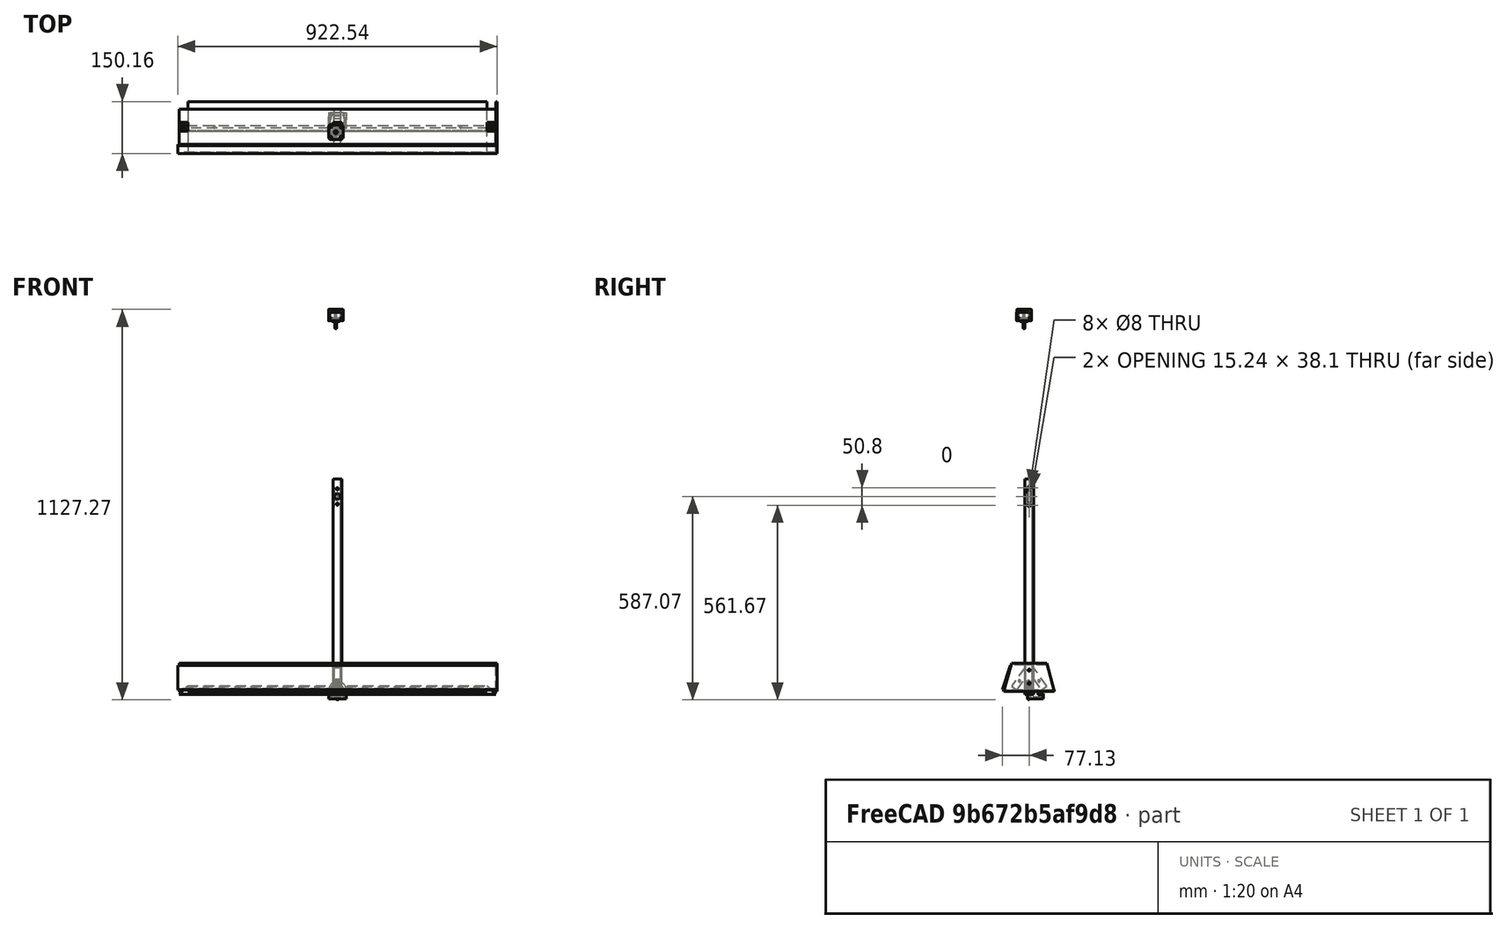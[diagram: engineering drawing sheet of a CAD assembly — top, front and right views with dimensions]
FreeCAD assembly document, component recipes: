
FREECAD ASSEMBLY — COMPONENT RECIPES ("Frame")

This assembly document has 15 components, labeled P0..P14 below (a component is one placed body or linked part). 14 of them carry a construction recipe — the FreeCAD feature program that regenerates the part from scratch, quoted from this document or its linked companion documents; the rest are supplied as boundary geometry only. No exploded tour is included for this assembly.
COMPONENT P0 — recipe-attached ("Base Extrusion", modeled in this document).
Construction recipe (the document's own serialized feature program — sketch geometry with constraints, then the solid features built on it; lengths are millimeters unless a unit is written):

FEATURE [Sketcher::SketchObject] Sketch
  FullyConstrained = true
  MapMode = 5
  Support = -> [XY_Plane]
  sketch-geometry (15):
    g0: LineSegment StartX=-12.7 StartY=-12.7 StartZ=0 EndX=-12.7 EndY=12.7 EndZ=0
    g1: LineSegment StartX=-12.7 StartY=12.7 StartZ=0 EndX=12.7 EndY=12.7 EndZ=0
    g2: LineSegment StartX=12.7 StartY=12.7 StartZ=0 EndX=12.7 EndY=-12.7 EndZ=0
    g3: LineSegment StartX=12.7 StartY=-12.7 StartZ=0 EndX=-12.7 EndY=-12.7 EndZ=0
    g4: GeomPoint X=0 Y=0 Z=0
    g5: ArcOfCircle CenterX=-6.35 CenterY=-6.35 CenterZ=0 NormalX=0 NormalY=0 NormalZ=1 AngleXU=0 Radius=3.175 StartAngle=3.14159 EndAngle=4.71239
    g6: LineSegment StartX=-9.525 StartY=-6.35 StartZ=0 EndX=-9.525 EndY=6.35 EndZ=0
    g7: ArcOfCircle CenterX=-6.35 CenterY=6.35 CenterZ=0 NormalX=0 NormalY=0 NormalZ=1 AngleXU=0 Radius=3.175 StartAngle=1.5708 EndAngle=3.14159
    g8: LineSegment StartX=-6.35 StartY=9.525 StartZ=0 EndX=6.35 EndY=9.525 EndZ=0
    g9: ArcOfCircle CenterX=6.35 CenterY=6.35 CenterZ=0 NormalX=0 NormalY=0 NormalZ=1 AngleXU=0 Radius=3.175 StartAngle=3e-16 EndAngle=1.5708
    g10: LineSegment StartX=9.525 StartY=6.35 StartZ=0 EndX=9.525 EndY=-6.35 EndZ=0
    g11: ArcOfCircle CenterX=6.35 CenterY=-6.35 CenterZ=0 NormalX=0 NormalY=0 NormalZ=1 AngleXU=0 Radius=3.175 StartAngle=4.71239 EndAngle=6.28319
    g12: LineSegment StartX=6.35 StartY=-9.525 StartZ=0 EndX=-6.35 EndY=-9.525 EndZ=0
    g13: GeomPoint X=-9.525 Y=-9.525 Z=0
    g14: GeomPoint X=9.525 Y=9.525 Z=0
  constraints (35):
    c: Coincident(g0,g1)
    c: Coincident(g1,g2)
    c: Coincident(g2,g3)
    c: Coincident(g3,g0)
    c: Horizontal(g1)
    c: Horizontal(g3)
    c: Vertical(g0)
    c: Vertical(g2)
    c: Symmetric(g1,g0,g4)
    c: Coincident(g4,g-1)
    c: Equal(g1,g2)
    c: Distance(g1) = 25.4
    c: Tangent(g5,g6) = 1.5708
    c: Tangent(g6,g7) = 1.5708
    c: Tangent(g7,g8) = 1.5708
    c: Tangent(g8,g9) = 1.5708
    c: Tangent(g9,g10) = 1.5708
    c: Tangent(g10,g11) = 1.5708
    c: Tangent(g11,g12) = 1.5708
    c: Tangent(g12,g5) = 1.5708
    c: Horizontal(g8)
    c: Horizontal(g12)
    c: Vertical(g6)
    c: Vertical(g10)
    c: Equal(g5,g7)
    c: Equal(g7,g9)
    c: Equal(g9,g11)
    c: PointOnObject(g13,g6)
    c: PointOnObject(g13,g12)
    c: PointOnObject(g14,g8)
    c: PointOnObject(g14,g10)
    c: Radius(g9) = 3.175
    c: Symmetric(g7,g11,g4)
    c: Distance(g7,g1) = 3.175
    c: Equal(g8,g6)
FEATURE [PartDesign::Pad] Pad
  Direction = (0,0,1)
  Length = 609.6
  Length2 = 10
  Profile = -> Sketch
  ReferenceAxis = -> Sketch [N_Axis]
  Type = 0
FEATURE [PartDesign::Body] Body  label="Base Extrusion"
  Group = -> [Sketch,Pad]
  Origin = -> Origin
  Tip = -> Pad
COMPONENT P1 — recipe-attached ("Motor Extrusion", modeled in this document).
Construction recipe (the document's own serialized feature program — sketch geometry with constraints, then the solid features built on it; lengths are millimeters unless a unit is written):

FEATURE [Sketcher::SketchObject] Sketch001
  FullyConstrained = true
  MapMode = 5
  Support = -> [XY_Plane001]
  sketch-geometry (15):
    g0: LineSegment StartX=-12.7 StartY=-12.7 StartZ=0 EndX=-12.7 EndY=12.7 EndZ=0
    g1: LineSegment StartX=-12.7 StartY=12.7 StartZ=0 EndX=12.7 EndY=12.7 EndZ=0
    g2: LineSegment StartX=12.7 StartY=12.7 StartZ=0 EndX=12.7 EndY=-12.7 EndZ=0
    g3: LineSegment StartX=12.7 StartY=-12.7 StartZ=0 EndX=-12.7 EndY=-12.7 EndZ=0
    g4: GeomPoint X=0 Y=0 Z=0
    g5: ArcOfCircle CenterX=-6.35 CenterY=-6.35 CenterZ=0 NormalX=0 NormalY=0 NormalZ=1 AngleXU=0 Radius=3.175 StartAngle=3.14159 EndAngle=4.71239
    g6: LineSegment StartX=-9.525 StartY=-6.35 StartZ=0 EndX=-9.525 EndY=6.35 EndZ=0
    g7: ArcOfCircle CenterX=-6.35 CenterY=6.35 CenterZ=0 NormalX=0 NormalY=0 NormalZ=1 AngleXU=0 Radius=3.175 StartAngle=1.5708 EndAngle=3.14159
    g8: LineSegment StartX=-6.35 StartY=9.525 StartZ=0 EndX=6.35 EndY=9.525 EndZ=0
    g9: ArcOfCircle CenterX=6.35 CenterY=6.35 CenterZ=0 NormalX=0 NormalY=0 NormalZ=1 AngleXU=0 Radius=3.175 StartAngle=3e-16 EndAngle=1.5708
    g10: LineSegment StartX=9.525 StartY=6.35 StartZ=0 EndX=9.525 EndY=-6.35 EndZ=0
    g11: ArcOfCircle CenterX=6.35 CenterY=-6.35 CenterZ=0 NormalX=0 NormalY=0 NormalZ=1 AngleXU=0 Radius=3.175 StartAngle=4.71239 EndAngle=6.28319
    g12: LineSegment StartX=6.35 StartY=-9.525 StartZ=0 EndX=-6.35 EndY=-9.525 EndZ=0
    g13: GeomPoint X=-9.525 Y=-9.525 Z=0
    g14: GeomPoint X=9.525 Y=9.525 Z=0
  constraints (35):
    c: Coincident(g0,g1)
    c: Coincident(g1,g2)
    c: Coincident(g2,g3)
    c: Coincident(g3,g0)
    c: Horizontal(g1)
    c: Horizontal(g3)
    c: Vertical(g0)
    c: Vertical(g2)
    c: Symmetric(g1,g0,g4)
    c: Coincident(g4,g-1)
    c: Equal(g1,g2)
    c: Distance(g1) = 25.4
    c: Tangent(g5,g6) = 1.5708
    c: Tangent(g6,g7) = 1.5708
    c: Tangent(g7,g8) = 1.5708
    c: Tangent(g8,g9) = 1.5708
    c: Tangent(g9,g10) = 1.5708
    c: Tangent(g10,g11) = 1.5708
    c: Tangent(g11,g12) = 1.5708
    c: Tangent(g12,g5) = 1.5708
    c: Horizontal(g8)
    c: Horizontal(g12)
    c: Vertical(g6)
    c: Vertical(g10)
    c: Equal(g5,g7)
    c: Equal(g7,g9)
    c: Equal(g9,g11)
    c: PointOnObject(g13,g6)
    c: PointOnObject(g13,g12)
    c: PointOnObject(g14,g8)
    c: PointOnObject(g14,g10)
    c: Radius(g9) = 3.175
    c: Symmetric(g7,g11,g4)
    c: Distance(g7,g1) = 3.175
    c: Equal(g8,g6)
FEATURE [PartDesign::Pad] Pad001
  Direction = (0,0,1)
  Length = 609.6
  Length2 = 10
  Profile = -> Sketch001
  ReferenceAxis = -> Sketch001 [N_Axis]
  Type = 0
FEATURE [Sketcher::SketchObject] Sketch002
  ExternalGeometry = -> [Pad001]
  FullyConstrained = true
  MapMode = 5
  Placement = pos=(0,12.7,0) rot=(0,0.707107,0.707107;3.14159rad)
  Support = -> [Pad001]
  sketch-geometry (8):
    g0: LineSegment StartX=0 StartY=580.72 StartZ=0 EndX=-21.9203 EndY=558.8 EndZ=0
    g1: LineSegment StartX=-21.9203 StartY=558.8 StartZ=0 EndX=0 EndY=536.88 EndZ=0
    g2: LineSegment StartX=0 StartY=536.88 StartZ=0 EndX=21.9203 EndY=558.8 EndZ=0
    g3: LineSegment StartX=21.9203 StartY=558.8 StartZ=0 EndX=0 EndY=580.72 EndZ=0
    g4: LineSegment StartX=21.9203 StartY=558.8 StartZ=0 EndX=-21.9203 EndY=558.8 EndZ=0
    g5: Circle CenterX=0 CenterY=558.8 CenterZ=0 NormalX=0 NormalY=0 NormalZ=1 AngleXU=0 Radius=8.89
    g6: Circle CenterX=0 CenterY=580.72 CenterZ=0 NormalX=0 NormalY=0 NormalZ=1 AngleXU=0 Radius=1.6
    g7: Circle CenterX=0 CenterY=536.88 CenterZ=0 NormalX=0 NormalY=0 NormalZ=1 AngleXU=0 Radius=1.6
  constraints (21):
    c: PointOnObject(g0,g-2)
    c: Coincident(g1,g0)
    c: PointOnObject(g1,g-2)
    c: Coincident(g2,g1)
    c: Coincident(g3,g2)
    c: Coincident(g3,g0)
    c: Perpendicular(g3,g0)
    c: Perpendicular(g2,g1)
    c: Perpendicular(g1,g0)
    c: Coincident(g4,g2)
    c: Coincident(g4,g0)
    c: Horizontal(g4)
    c: Distance(g3) = 31
    c: PointOnObject(g5,g4)
    c: Coincident(g6,g0)
    c: Coincident(g7,g1)
    c: PointOnObject(g5,g-2)
    c: Equal(g7,g6)
    c: Diameter(g6) = 3.2
    c: Diameter(g5) = 17.78
    c: Distance(g5,g-3) = 50.8
FEATURE [PartDesign::Pocket] Pocket
  BaseFeature = -> Pad001
  Direction = (0,-1,2e-16)
  Length = 5.08
  Length2 = 5
  Profile = -> Sketch002
  ReferenceAxis = -> Sketch002 [N_Axis]
  Type = 0
FEATURE [Sketcher::SketchObject] Sketch003
  ExternalGeometry = -> [Pocket]
  FullyConstrained = true
  MapMode = 5
  Placement = pos=(-12.7,0,0) rot=(0.57735,-0.57735,-0.57735;2.0944rad)
  Support = -> [Pocket]
  sketch-geometry (2):
    g0: Circle CenterX=0 CenterY=584.2 CenterZ=0 NormalX=0 NormalY=0 NormalZ=1 AngleXU=0 Radius=4
    g1: Circle CenterX=0 CenterY=533.4 CenterZ=0 NormalX=0 NormalY=0 NormalZ=1 AngleXU=0 Radius=4
  constraints (6):
    c: PointOnObject(g0,g-2)
    c: PointOnObject(g1,g-2)
    c: Equal(g1,g0)
    c: Diameter(g0) = 8
    c: Distance(g0,g1) = 50.8
    c: Distance(g0,g-3) = 25.4
FEATURE [PartDesign::Pocket] Pocket001
  BaseFeature = -> Pocket
  Direction = (1,0,0)
  Length = 5
  Length2 = 5
  Profile = -> Sketch003
  ReferenceAxis = -> Sketch003 [N_Axis]
  Type = 1
FEATURE [Sketcher::SketchObject] Sketch004
  ExternalGeometry = -> [Pocket001]
  FullyConstrained = true
  MapMode = 5
  Placement = pos=(0,-12.7,0) rot=(1,0,0;1.5708rad)
  Support = -> [Pocket001]
  sketch-geometry (3):
    g0: LineSegment StartX=12.7 StartY=0 StartZ=0 EndX=-12.7 EndY=0 EndZ=0
    g1: LineSegment StartX=-12.7 StartY=0 StartZ=0 EndX=-12.7 EndY=25.4 EndZ=0
    g2: LineSegment StartX=-12.7 StartY=25.4 StartZ=0 EndX=12.7 EndY=0 EndZ=0
  constraints (7):
    c: Coincident(g0,g-3)
    c: Coincident(g1,g0)
    c: Vertical(g1)
    c: Coincident(g2,g1)
    c: Coincident(g2,g0)
    c: Equal(g1,g0)
    c: Coincident(g-4,g0)
FEATURE [PartDesign::Pocket] Pocket002
  BaseFeature = -> Pocket001
  Direction = (0,1,-2e-16)
  Length = 5
  Length2 = 5
  Profile = -> Sketch004
  ReferenceAxis = -> Sketch004 [N_Axis]
  Type = 1
FEATURE [PartDesign::CoordinateSystem] Local_CS  label="MotorWeldLCS"
  AttacherType = Attacher::AttachEngine3D
  MapMode = 45
  Placement = pos=(2.4e-14,-3.168e-13,12.7) rot=(0.357407,0.357407,0.862856;1.71777rad)
  Support = -> [Pocket002]
FEATURE [PartDesign::CoordinateSystem] Local_CS001  label="MotorLCS"
  AttacherType = Attacher::AttachEngine3D
  MapMode = 11
  Placement = pos=(0,12.7,558.8) rot=(0.57735,0.57735,0.57735;4.18879rad)
  Support = -> [Pocket002]
FEATURE [PartDesign::CoordinateSystem] Local_CS002  label="LowerRailLCS"
  AttacherType = Attacher::AttachEngine3D
  MapMode = 11
  Placement = pos=(12.7,0,533.4) rot=(0,-1,0;1.5708rad)
  Support = -> [Pocket002]
FEATURE [PartDesign::CoordinateSystem] Local_CS003  label="UpperRailLCS"
  AttacherType = Attacher::AttachEngine3D
  MapMode = 11
  Placement = pos=(12.7,0,584.2) rot=(0,-1,0;1.5708rad)
  Support = -> [Pocket002]
FEATURE [Sketcher::SketchObject] Sketch010
  ExternalGeometry = -> [Pocket002]
  FullyConstrained = true
  MapMode = 5
  Placement = pos=(12.7,0,0) rot=(0.57735,0.57735,0.57735;2.0944rad)
  Support = -> [Pocket002]
  sketch-geometry (12):
    g0: ArcOfCircle CenterX=-2.8575 CenterY=544.513 CenterZ=0 NormalX=0 NormalY=0 NormalZ=1 AngleXU=0 Radius=4.7625 StartAngle=3.14159 EndAngle=4.71239
    g1: LineSegment StartX=-7.62 StartY=544.513 StartZ=0 EndX=-7.62 EndY=573.088 EndZ=0
    g2: ArcOfCircle CenterX=-2.8575 CenterY=573.088 CenterZ=0 NormalX=0 NormalY=0 NormalZ=1 AngleXU=0 Radius=4.7625 StartAngle=1.5708 EndAngle=3.14159
    g3: LineSegment StartX=-2.8575 StartY=577.85 StartZ=0 EndX=2.8575 EndY=577.85 EndZ=0
    g4: ArcOfCircle CenterX=2.8575 CenterY=573.088 CenterZ=0 NormalX=0 NormalY=0 NormalZ=1 AngleXU=0 Radius=4.7625 StartAngle=-5.3e-15 EndAngle=1.5708
    g5: LineSegment StartX=7.62 StartY=573.088 StartZ=0 EndX=7.62 EndY=544.513 EndZ=0
    g6: ArcOfCircle CenterX=2.8575 CenterY=544.513 CenterZ=0 NormalX=0 NormalY=0 NormalZ=1 AngleXU=0 Radius=4.7625 StartAngle=4.71239 EndAngle=6.28319
    g7: LineSegment StartX=2.8575 StartY=539.75 StartZ=0 EndX=-2.8575 EndY=539.75 EndZ=0
    g8: GeomPoint X=-7.62 Y=539.75 Z=0
    g9: GeomPoint X=7.62 Y=577.85 Z=0
    g10: LineSegment StartX=0 StartY=584.2 StartZ=0 EndX=0 EndY=577.85 EndZ=0
    g11: LineSegment StartX=0 StartY=533.4 StartZ=0 EndX=0 EndY=539.75 EndZ=0
  constraints (29):
    c: Tangent(g0,g1) = 1.5708
    c: Tangent(g1,g2) = 1.5708
    c: Tangent(g2,g3) = 1.5708
    c: Tangent(g3,g4) = 1.5708
    c: Tangent(g4,g5) = 1.5708
    c: Tangent(g5,g6) = 1.5708
    c: Tangent(g6,g7) = 1.5708
    c: Tangent(g7,g0) = 1.5708
    c: Horizontal(g3)
    c: Horizontal(g7)
    c: Vertical(g1)
    c: Vertical(g5)
    c: Equal(g0,g2)
    c: Equal(g4,g6)
    c: PointOnObject(g8,g1)
    c: PointOnObject(g8,g7)
    c: PointOnObject(g9,g3)
    c: PointOnObject(g9,g5)
    c: Radius(g4) = 4.7625
    c: Symmetric(g4,g2,g-2)
    c: Distance(g1,g4) = 15.24
    c: Coincident(g10,g-3)
    c: PointOnObject(g10,g3)
    c: Vertical(g10)
    c: Coincident(g11,g-4)
    c: PointOnObject(g11,g7)
    c: Vertical(g11)
    c: Equal(g11,g10)
    c: Distance(g10) = 6.35
FEATURE [PartDesign::Pocket] Pocket006
  BaseFeature = -> Pocket002
  Direction = (-1,0,0)
  Length = 5
  Length2 = 5
  Profile = -> Sketch010
  ReferenceAxis = -> Sketch010 [N_Axis]
  Type = 1
FEATURE [PartDesign::Plane] DatumPlane
  AttachmentOffset = pos=(0,0,-3.175) rot=(0,0,1;0rad)
  Length = 60
  MapMode = 5
  Placement = pos=(-9.525,0,0) rot=(0.57735,-0.57735,-0.57735;2.0944rad)
  ResizeMode = 0
  Support = -> [Pocket006]
  Width = 60
FEATURE [Sketcher::SketchObject] Sketch014
  ExternalGeometry = -> [Pocket006]
  FullyConstrained = true
  MapMode = 5
  Placement = pos=(-9.525,0,0) rot=(0.57735,-0.57735,-0.57735;2.0944rad)
  Support = -> [DatumPlane]
  sketch-geometry (9):
    g0: LineSegment StartX=12.7 StartY=31.75 StartZ=0 EndX=12.7 EndY=64.9627 EndZ=0
    g1: LineSegment StartX=12.7 StartY=64.9627 StartZ=0 EndX=50.5364 EndY=10.9266 EndZ=0
    g2: LineSegment StartX=50.5364 StartY=10.9266 StartZ=0 EndX=34.9316 EndY=0 EndZ=0
    g3: LineSegment StartX=34.9316 StartY=0 StartZ=0 EndX=12.7 EndY=31.75 EndZ=0
    g4: LineSegment StartX=-12.7 StartY=64.9627 StartZ=0 EndX=-12.7 EndY=31.75 EndZ=0
    g5: LineSegment StartX=-12.7 StartY=31.75 StartZ=0 EndX=-34.9316 EndY=-7.1e-15 EndZ=0
    g6: LineSegment StartX=-34.9316 StartY=-7.1e-15 StartZ=0 EndX=-50.5364 EndY=10.9266 EndZ=0
    g7: LineSegment StartX=-50.5364 StartY=10.9266 StartZ=0 EndX=-12.7 EndY=64.9627 EndZ=0
    g8: LineSegment StartX=12.7 StartY=31.75 StartZ=0 EndX=-12.7 EndY=31.75 EndZ=0
  constraints (26):
    c: Vertical(g0)
    c: Coincident(g1,g0)
    c: Coincident(g2,g1)
    c: Coincident(g3,g2)
    c: Coincident(g3,g0)
    c: Vertical(g4)
    c: Coincident(g5,g4)
    c: Coincident(g6,g5)
    c: Coincident(g7,g6)
    c: Coincident(g7,g4)
    c: Equal(g4,g0)
    c: Perpendicular(g6,g5)
    c: Perpendicular(g7,g6)
    c: Perpendicular(g2,g3)
    c: Perpendicular(g1,g2)
    c: Coincident(g8,g0)
    c: Horizontal(g8)
    c: Coincident(g4,g8)
    c: PointOnObject(g4,g-4)
    c: PointOnObject(g0,g-3)
    c: Distance(g-3,g0) = 6.35
    c: Distance(g2) = 19.05
    c: Equal(g6,g2)
    c: Equal(g3,g5)
    c: PointOnObject(g2,g-1)
    c: Angle(g3,g-3) = 2.53073
FEATURE [PartDesign::Pad] Pad004
  BaseFeature = -> Pocket006
  Direction = (-1,0,0)
  Length = 19.05
  Length2 = 10
  Profile = -> Sketch014
  ReferenceAxis = -> Sketch014 [N_Axis]
  Reversed = true
  Type = 0
FEATURE [Sketcher::SketchObject] Sketch020
  ExternalGeometry = -> [Pad004]
  FullyConstrained = true
  MapMode = 5
  Placement = pos=(0,-12.7,0) rot=(1,0,0;1.5708rad)
  Support = -> [Pad004]
  sketch-geometry (2):
    g0: Circle CenterX=0 CenterY=536.88 CenterZ=0 NormalX=0 NormalY=0 NormalZ=1 AngleXU=0 Radius=3.302
    g1: Circle CenterX=0 CenterY=580.72 CenterZ=0 NormalX=0 NormalY=0 NormalZ=1 AngleXU=0 Radius=3.302
  constraints (4):
    c: Coincident(g0,g-5)
    c: Coincident(g1,g-3)
    c: Equal(g1,g0)
    c: Diameter(g1) = 6.604
FEATURE [PartDesign::Pocket] Pocket012
  BaseFeature = -> Pad004
  Direction = (0,1,-2e-16)
  Length = 7.62
  Length2 = 5
  Profile = -> Sketch020
  ReferenceAxis = -> Sketch020 [N_Axis]
  Type = 0
FEATURE [Sketcher::SketchObject] Sketch021
  ExternalGeometry = -> [Pocket012]
  FullyConstrained = true
  MapMode = 5
  Placement = pos=(9.525,0,0) rot=(0.57735,0.57735,0.57735;2.0944rad)
  Support = -> [Pocket012]
  sketch-geometry (4):
    g0: LineSegment StartX=-42.734 StartY=5.46332 StartZ=0 EndX=-28.1652 EndY=26.2698 EndZ=0
    g1: LineSegment StartX=42.734 StartY=5.46332 StartZ=0 EndX=28.1652 EndY=26.2698 EndZ=0
    g2: Circle CenterX=-28.1652 CenterY=26.2698 CenterZ=0 NormalX=0 NormalY=0 NormalZ=1 AngleXU=0 Radius=3.175
    g3: Circle CenterX=28.1652 CenterY=26.2698 CenterZ=0 NormalX=0 NormalY=0 NormalZ=1 AngleXU=0 Radius=3.175
  constraints (10):
    c: Symmetric(g-3,g-3,g0)
    c: Symmetric(g-4,g-4,g1)
    c: Equal(g0,g1)
    c: Perpendicular(g-3,g0)
    c: Perpendicular(g-4,g1)
    c: Distance(g1) = 25.4
    c: Coincident(g2,g0)
    c: Coincident(g3,g1)
    c: Equal(g3,g2)
    c: Diameter(g2) = 6.35
FEATURE [PartDesign::Pocket] Pocket013
  BaseFeature = -> Pocket012
  Direction = (-1,0,0)
  Length = 5
  Length2 = 5
  Profile = -> Sketch021
  ReferenceAxis = -> Sketch021 [N_Axis]
  Type = 1
FEATURE [PartDesign::Body] Body001  label="Motor Extrusion"
  Group = -> [Sketch001,Pad001,Sketch002,Pocket,Sketch003,Pocket001,Sketch004,Pocket002,Local_CS,Local_CS001,Local_CS002,Local_CS003,Sketch010,Pocket006,DatumPlane,Sketch014,Pad004,Sketch020,Pocket012,Sketch021,Pocket013]
  Origin = -> Origin001
  Tip = -> Pocket013
COMPONENT P2 — recipe-attached ("Endplate Extrusion", modeled in this document).
Construction recipe (the document's own serialized feature program — sketch geometry with constraints, then the solid features built on it; lengths are millimeters unless a unit is written):

FEATURE [Sketcher::SketchObject] Sketch005
  FullyConstrained = true
  MapMode = 5
  Support = -> [XY_Plane002]
  sketch-geometry (15):
    g0: LineSegment StartX=-12.7 StartY=-12.7 StartZ=0 EndX=-12.7 EndY=12.7 EndZ=0
    g1: LineSegment StartX=-12.7 StartY=12.7 StartZ=0 EndX=12.7 EndY=12.7 EndZ=0
    g2: LineSegment StartX=12.7 StartY=12.7 StartZ=0 EndX=12.7 EndY=-12.7 EndZ=0
    g3: LineSegment StartX=12.7 StartY=-12.7 StartZ=0 EndX=-12.7 EndY=-12.7 EndZ=0
    g4: GeomPoint X=0 Y=0 Z=0
    g5: ArcOfCircle CenterX=-6.35 CenterY=-6.35 CenterZ=0 NormalX=0 NormalY=0 NormalZ=1 AngleXU=0 Radius=3.175 StartAngle=3.14159 EndAngle=4.71239
    g6: LineSegment StartX=-9.525 StartY=-6.35 StartZ=0 EndX=-9.525 EndY=6.35 EndZ=0
    g7: ArcOfCircle CenterX=-6.35 CenterY=6.35 CenterZ=0 NormalX=0 NormalY=0 NormalZ=1 AngleXU=0 Radius=3.175 StartAngle=1.5708 EndAngle=3.14159
    g8: LineSegment StartX=-6.35 StartY=9.525 StartZ=0 EndX=6.35 EndY=9.525 EndZ=0
    g9: ArcOfCircle CenterX=6.35 CenterY=6.35 CenterZ=0 NormalX=0 NormalY=0 NormalZ=1 AngleXU=0 Radius=3.175 StartAngle=3e-16 EndAngle=1.5708
    g10: LineSegment StartX=9.525 StartY=6.35 StartZ=0 EndX=9.525 EndY=-6.35 EndZ=0
    g11: ArcOfCircle CenterX=6.35 CenterY=-6.35 CenterZ=0 NormalX=0 NormalY=0 NormalZ=1 AngleXU=0 Radius=3.175 StartAngle=4.71239 EndAngle=6.28319
    g12: LineSegment StartX=6.35 StartY=-9.525 StartZ=0 EndX=-6.35 EndY=-9.525 EndZ=0
    g13: GeomPoint X=-9.525 Y=-9.525 Z=0
    g14: GeomPoint X=9.525 Y=9.525 Z=0
  constraints (35):
    c: Coincident(g0,g1)
    c: Coincident(g1,g2)
    c: Coincident(g2,g3)
    c: Coincident(g3,g0)
    c: Horizontal(g1)
    c: Horizontal(g3)
    c: Vertical(g0)
    c: Vertical(g2)
    c: Symmetric(g1,g0,g4)
    c: Coincident(g4,g-1)
    c: Equal(g1,g2)
    c: Distance(g1) = 25.4
    c: Tangent(g5,g6) = 1.5708
    c: Tangent(g6,g7) = 1.5708
    c: Tangent(g7,g8) = 1.5708
    c: Tangent(g8,g9) = 1.5708
    c: Tangent(g9,g10) = 1.5708
    c: Tangent(g10,g11) = 1.5708
    c: Tangent(g11,g12) = 1.5708
    c: Tangent(g12,g5) = 1.5708
    c: Horizontal(g8)
    c: Horizontal(g12)
    c: Vertical(g6)
    c: Vertical(g10)
    c: Equal(g5,g7)
    c: Equal(g7,g9)
    c: Equal(g9,g11)
    c: PointOnObject(g13,g6)
    c: PointOnObject(g13,g12)
    c: PointOnObject(g14,g8)
    c: PointOnObject(g14,g10)
    c: Radius(g9) = 3.175
    c: Symmetric(g7,g11,g4)
    c: Distance(g7,g1) = 3.175
    c: Equal(g8,g6)
FEATURE [PartDesign::Pad] Pad002
  Direction = (0,0,1)
  Length = 609.6
  Length2 = 10
  Profile = -> Sketch005
  ReferenceAxis = -> Sketch005 [N_Axis]
  Type = 0
FEATURE [Sketcher::SketchObject] Sketch006
  ExternalGeometry = -> [Pad002]
  FullyConstrained = true
  MapMode = 5
  Placement = pos=(12.7,0,0) rot=(0.57735,0.57735,0.57735;2.0944rad)
  Support = -> [Pad002]
  sketch-geometry (2):
    g0: Circle CenterX=0 CenterY=584.2 CenterZ=0 NormalX=0 NormalY=0 NormalZ=1 AngleXU=0 Radius=4
    g1: Circle CenterX=0 CenterY=533.4 CenterZ=0 NormalX=0 NormalY=0 NormalZ=1 AngleXU=0 Radius=4
  constraints (6):
    c: PointOnObject(g0,g-2)
    c: PointOnObject(g1,g-2)
    c: Equal(g1,g0)
    c: Diameter(g0) = 8
    c: Distance(g0,g-3) = 25.4
    c: Distance(g0,g1) = 50.8
FEATURE [PartDesign::Pocket] Pocket003
  BaseFeature = -> Pad002
  Direction = (-1,0,0)
  Length = 5
  Length2 = 5
  Profile = -> Sketch006
  ReferenceAxis = -> Sketch006 [N_Axis]
  Type = 1
FEATURE [Sketcher::SketchObject] Sketch007
  ExternalGeometry = -> [Pocket003]
  FullyConstrained = true
  MapMode = 5
  Placement = pos=(0,-12.7,0) rot=(1,0,0;1.5708rad)
  Support = -> [Pocket003]
  sketch-geometry (3):
    g0: LineSegment StartX=12.7 StartY=25.4 StartZ=0 EndX=-12.7 EndY=0 EndZ=0
    g1: LineSegment StartX=12.7 StartY=25.4 StartZ=0 EndX=12.7 EndY=0 EndZ=0
    g2: LineSegment StartX=12.7 StartY=0 StartZ=0 EndX=-12.7 EndY=0 EndZ=0
  constraints (7):
    c: PointOnObject(g0,g-4)
    c: Coincident(g1,g0)
    c: Coincident(g1,g-4)
    c: Coincident(g2,g1)
    c: Coincident(g2,g0)
    c: Equal(g1,g2)
    c: Coincident(g0,g-3)
FEATURE [PartDesign::Pocket] Pocket004
  BaseFeature = -> Pocket003
  Direction = (0,1,-2e-16)
  Length = 5
  Length2 = 5
  Profile = -> Sketch007
  ReferenceAxis = -> Sketch007 [N_Axis]
  Type = 1
FEATURE [PartDesign::CoordinateSystem] Local_CS004  label="EndWeldLCS"
  AttacherType = Attacher::AttachEngine3D
  MapMode = 45
  Placement = pos=(2.49e-14,3.02e-14,12.7) rot=(-0.357407,-0.357407,0.862856;1.71777rad)
  Support = -> [Pocket004]
FEATURE [Sketcher::SketchObject] Sketch011
  ExternalGeometry = -> [Pocket004]
  FullyConstrained = true
  MapMode = 5
  Placement = pos=(-12.7,0,0) rot=(0.57735,-0.57735,-0.57735;2.0944rad)
  Support = -> [Pocket004]
  sketch-geometry (12):
    g0: ArcOfCircle CenterX=-2.8575 CenterY=544.513 CenterZ=0 NormalX=0 NormalY=0 NormalZ=1 AngleXU=0 Radius=4.7625 StartAngle=3.14159 EndAngle=4.71239
    g1: LineSegment StartX=-7.62 StartY=544.513 StartZ=0 EndX=-7.62 EndY=573.087 EndZ=0
    g2: ArcOfCircle CenterX=-2.8575 CenterY=573.087 CenterZ=0 NormalX=0 NormalY=0 NormalZ=1 AngleXU=0 Radius=4.7625 StartAngle=1.5708 EndAngle=3.14159
    g3: LineSegment StartX=-2.8575 StartY=577.85 StartZ=0 EndX=2.8575 EndY=577.85 EndZ=0
    g4: ArcOfCircle CenterX=2.8575 CenterY=573.087 CenterZ=0 NormalX=0 NormalY=0 NormalZ=1 AngleXU=0 Radius=4.7625 StartAngle=-8.9e-15 EndAngle=1.5708
    g5: LineSegment StartX=7.62 StartY=573.087 StartZ=0 EndX=7.62 EndY=544.513 EndZ=0
    g6: ArcOfCircle CenterX=2.8575 CenterY=544.513 CenterZ=0 NormalX=0 NormalY=0 NormalZ=1 AngleXU=0 Radius=4.7625 StartAngle=4.71239 EndAngle=6.28319
    g7: LineSegment StartX=2.8575 StartY=539.75 StartZ=0 EndX=-2.8575 EndY=539.75 EndZ=0
    g8: GeomPoint X=-7.62 Y=539.75 Z=0
    g9: GeomPoint X=7.62 Y=577.85 Z=0
    g10: LineSegment StartX=0 StartY=577.85 StartZ=0 EndX=0 EndY=584.2 EndZ=0
    g11: LineSegment StartX=0 StartY=539.75 StartZ=0 EndX=0 EndY=533.4 EndZ=0
  constraints (29):
    c: Tangent(g0,g1) = 1.5708
    c: Tangent(g1,g2) = 1.5708
    c: Tangent(g2,g3) = 1.5708
    c: Tangent(g3,g4) = 1.5708
    c: Tangent(g4,g5) = 1.5708
    c: Tangent(g5,g6) = 1.5708
    c: Tangent(g6,g7) = 1.5708
    c: Tangent(g7,g0) = 1.5708
    c: Horizontal(g3)
    c: Vertical(g1)
    c: Vertical(g5)
    c: Equal(g0,g2)
    c: Equal(g2,g4)
    c: Equal(g4,g6)
    c: PointOnObject(g8,g1)
    c: PointOnObject(g8,g7)
    c: PointOnObject(g9,g3)
    c: PointOnObject(g9,g5)
    c: Symmetric(g6,g0,g-2)
    c: Radius(g6) = 4.7625
    c: PointOnObject(g10,g3)
    c: Coincident(g10,g-3)
    c: Vertical(g10)
    c: PointOnObject(g11,g7)
    c: Coincident(g11,g-4)
    c: Vertical(g11)
    c: Equal(g11,g10)
    c: Distance(g10) = 6.35
    c: Distance(g4,g1) = 15.24
FEATURE [PartDesign::Pocket] Pocket007
  BaseFeature = -> Pocket004
  Direction = (1,0,0)
  Length = 5
  Length2 = 5
  Profile = -> Sketch011
  ReferenceAxis = -> Sketch011 [N_Axis]
  Type = 1
FEATURE [Sketcher::SketchObject] Sketch012
  ExternalGeometry = -> [Pocket007]
  FullyConstrained = true
  MapMode = 5
  Placement = pos=(0,-12.7,0) rot=(1,0,0;1.5708rad)
  Support = -> [Pocket007]
  sketch-geometry (2):
    g0: Circle CenterX=0 CenterY=558.8 CenterZ=0 NormalX=0 NormalY=0 NormalZ=1 AngleXU=0 Radius=8.255
    g1: LineSegment StartX=0 StartY=558.8 StartZ=0 EndX=-12.7 EndY=558.8 EndZ=0
  constraints (5):
    c: PointOnObject(g0,g-2)
    c: Diameter(g0) = 16.51
    c: Coincident(g1,g0)
    c: Horizontal(g1)
    c: Symmetric(g-3,g-3,g1)
FEATURE [PartDesign::Pocket] Pocket008
  BaseFeature = -> Pocket007
  Direction = (0,1,-2e-16)
  Length = 5.08
  Length2 = 5
  Profile = -> Sketch012
  ReferenceAxis = -> Sketch012 [N_Axis]
  Type = 0
FEATURE [Sketcher::SketchObject] Sketch013
  ExternalGeometry = -> [Pocket008]
  FullyConstrained = true
  MapMode = 5
  Placement = pos=(0,-12.7,0) rot=(1,0,0;1.5708rad)
  Support = -> [Pocket008]
  sketch-geometry (1):
    g0: Circle CenterX=0 CenterY=558.8 CenterZ=0 NormalX=0 NormalY=0 NormalZ=1 AngleXU=0 Radius=1.5875
  constraints (2):
    c: Coincident(g0,g-3)
    c: Diameter(g0) = 3.175
FEATURE [PartDesign::Pocket] Pocket009
  BaseFeature = -> Pocket008
  Direction = (0,1,-2e-16)
  Length = 5
  Length2 = 5
  Profile = -> Sketch013
  ReferenceAxis = -> Sketch013 [N_Axis]
  Type = 1
FEATURE [PartDesign::CoordinateSystem] Local_CS011  label="UpperRail"
  AttacherType = Attacher::AttachEngine3D
  MapMode = 11
  Placement = pos=(-12.7,0,584.2) rot=(0.707107,0,0.707107;3.14159rad)
  Support = -> [Pocket009]
FEATURE [PartDesign::CoordinateSystem] Local_CS012  label="LowerRail"
  AttacherType = Attacher::AttachEngine3D
  MapMode = 11
  Placement = pos=(-12.7,0,533.4) rot=(0.707107,0,0.707107;3.14159rad)
  Support = -> [Pocket009]
FEATURE [PartDesign::CoordinateSystem] Local_CS015  label="Eccentric001"
  AttacherType = Attacher::AttachEngine3D
  MapMode = 11
  Placement = pos=(0,9.525,558.8) rot=(0.57735,-0.57735,0.57735;2.0944rad)
  Support = -> [Pocket009]
FEATURE [PartDesign::Body] Body002  label="Endplate Extrusion"
  Group = -> [Sketch005,Pad002,Sketch006,Pocket003,Sketch007,Pocket004,Local_CS004,Sketch011,Pocket007,Sketch012,Pocket008,Sketch013,Pocket009,Local_CS011,Local_CS012,Local_CS015]
  Origin = -> Origin002
  Tip = -> Pocket009
COMPONENT P3 — recipe-attached ("Lower Extrusion", modeled in this document).
Construction recipe (the document's own serialized feature program — sketch geometry with constraints, then the solid features built on it; lengths are millimeters unless a unit is written):

FEATURE [Sketcher::SketchObject] Sketch008
  FullyConstrained = true
  MapMode = 5
  Placement = pos=(0,0,0) rot=(0.57735,0.57735,0.57735;2.0944rad)
  Support = -> [YZ_Plane003]
  sketch-geometry (15):
    g0: LineSegment StartX=-12.7 StartY=-12.7 StartZ=0 EndX=-12.7 EndY=12.7 EndZ=0
    g1: LineSegment StartX=-12.7 StartY=12.7 StartZ=0 EndX=12.7 EndY=12.7 EndZ=0
    g2: LineSegment StartX=12.7 StartY=12.7 StartZ=0 EndX=12.7 EndY=-12.7 EndZ=0
    g3: LineSegment StartX=12.7 StartY=-12.7 StartZ=0 EndX=-12.7 EndY=-12.7 EndZ=0
    g4: GeomPoint X=0 Y=0 Z=0
    g5: ArcOfCircle CenterX=-6.35 CenterY=-6.35 CenterZ=0 NormalX=0 NormalY=0 NormalZ=1 AngleXU=0 Radius=3.175 StartAngle=3.14159 EndAngle=4.71239
    g6: LineSegment StartX=-9.525 StartY=-6.35 StartZ=0 EndX=-9.525 EndY=6.35 EndZ=0
    g7: ArcOfCircle CenterX=-6.35 CenterY=6.35 CenterZ=0 NormalX=0 NormalY=0 NormalZ=1 AngleXU=0 Radius=3.175 StartAngle=1.5708 EndAngle=3.14159
    g8: LineSegment StartX=-6.35 StartY=9.525 StartZ=0 EndX=6.35 EndY=9.525 EndZ=0
    g9: ArcOfCircle CenterX=6.35 CenterY=6.35 CenterZ=0 NormalX=0 NormalY=0 NormalZ=1 AngleXU=0 Radius=3.175 StartAngle=2e-16 EndAngle=1.5708
    g10: LineSegment StartX=9.525 StartY=6.35 StartZ=0 EndX=9.525 EndY=-6.35 EndZ=0
    g11: ArcOfCircle CenterX=6.35 CenterY=-6.35 CenterZ=0 NormalX=0 NormalY=0 NormalZ=1 AngleXU=0 Radius=3.175 StartAngle=4.71239 EndAngle=6.28319
    g12: LineSegment StartX=6.35 StartY=-9.525 StartZ=0 EndX=-6.35 EndY=-9.525 EndZ=0
    g13: GeomPoint X=-9.525 Y=-9.525 Z=0
    g14: GeomPoint X=9.525 Y=9.525 Z=0
  constraints (35):
    c: Coincident(g0,g1)
    c: Coincident(g1,g2)
    c: Coincident(g2,g3)
    c: Coincident(g3,g0)
    c: Horizontal(g1)
    c: Horizontal(g3)
    c: Vertical(g0)
    c: Vertical(g2)
    c: Symmetric(g1,g0,g4)
    c: Coincident(g4,g-1)
    c: Tangent(g5,g6) = 1.5708
    c: Tangent(g6,g7) = 1.5708
    c: Tangent(g7,g8) = 1.5708
    c: Tangent(g8,g9) = 1.5708
    c: Tangent(g9,g10) = 1.5708
    c: Tangent(g10,g11) = 1.5708
    c: Tangent(g11,g12) = 1.5708
    c: Tangent(g12,g5) = 1.5708
    c: Horizontal(g8)
    c: Horizontal(g12)
    c: Vertical(g6)
    c: Vertical(g10)
    c: Equal(g5,g7)
    c: Equal(g7,g9)
    c: Equal(g9,g11)
    c: PointOnObject(g13,g6)
    c: PointOnObject(g13,g12)
    c: PointOnObject(g14,g8)
    c: PointOnObject(g14,g10)
    c: Equal(g8,g6)
    c: Equal(g1,g0)
    c: Symmetric(g9,g5,g4)
    c: Radius(g11) = 3.175
    c: Distance(g10,g2) = 3.175
    c: Distance(g2) = 25.4
FEATURE [PartDesign::Pad] Pad003  label="OverallLength"
  Direction = (1,-2e-16,3e-16)
  Length = 914.4
  Length2 = 10
  Midplane = true
  Placement = pos=(0,0,0) rot=(0.57735,0.57735,0.57735;2.0944rad)
  Profile = -> Sketch008
  ReferenceAxis = -> Sketch008 [N_Axis]
  Type = 0
FEATURE [Sketcher::SketchObject] Sketch009
  ExternalGeometry = -> [Pad003]
  FullyConstrained = true
  MapMode = 5
  Placement = pos=(-5.6e-15,-12.7,2.8e-15) rot=(-0.57735,-0.57735,0.57735;4.18879rad)
  Support = -> [Pad003]
  sketch-geometry (6):
    g0: LineSegment StartX=12.7 StartY=457.2 StartZ=0 EndX=-12.7 EndY=457.2 EndZ=0
    g1: LineSegment StartX=-12.7 StartY=457.2 StartZ=0 EndX=-12.7 EndY=431.8 EndZ=0
    g2: LineSegment StartX=-12.7 StartY=431.8 StartZ=0 EndX=12.7 EndY=457.2 EndZ=0
    g3: LineSegment StartX=12.7 StartY=-457.2 StartZ=0 EndX=-12.7 EndY=-457.2 EndZ=0
    g4: LineSegment StartX=-12.7 StartY=-457.2 StartZ=0 EndX=-12.7 EndY=-431.8 EndZ=0
    g5: LineSegment StartX=-12.7 StartY=-431.8 StartZ=0 EndX=12.7 EndY=-457.2 EndZ=0
  constraints (14):
    c: Coincident(g0,g-5)
    c: Coincident(g0,g-4)
    c: Coincident(g1,g0)
    c: PointOnObject(g1,g-4)
    c: Coincident(g2,g1)
    c: Coincident(g2,g0)
    c: Coincident(g3,g-3)
    c: Coincident(g3,g-4)
    c: Coincident(g4,g3)
    c: PointOnObject(g4,g-4)
    c: Coincident(g5,g4)
    c: Coincident(g5,g3)
    c: Equal(g1,g0)
    c: Equal(g0,g4)
FEATURE [PartDesign::Pocket] Pocket005
  BaseFeature = -> Pad003
  Direction = (4e-16,1,-2e-16)
  Length = 5
  Length2 = 5
  Placement = pos=(0,0,0) rot=(0.57735,0.57735,0.57735;2.0944rad)
  Profile = -> Sketch009
  ReferenceAxis = -> Sketch009 [N_Axis]
  Type = 1
FEATURE [PartDesign::CoordinateSystem] Local_CS005  label="LeftLCS"
  AttacherType = Attacher::AttachEngine3D
  MapMode = 45
  Placement = pos=(-444.5,3.845e-13,-8.53e-14) rot=(-0.357407,-0.357407,0.862856;1.71777rad)
  Support = -> [Pocket005]
FEATURE [PartDesign::CoordinateSystem] Local_CS006  label="RightLCS"
  AttacherType = Attacher::AttachEngine3D
  MapMode = 45
  Placement = pos=(444.5,-6.185e-13,0) rot=(0.357407,0.357407,0.862856;1.71777rad)
  Support = -> [Pocket005]
FEATURE [PartDesign::CoordinateSystem] Local_CS007
  AttacherType = Attacher::AttachEngine3D
  MapMode = 5
  Placement = pos=(3.6e-15,-5.6e-15,-12.7) rot=(0.707107,0.707107,0;3.14159rad)
  Support = -> [Pocket005]
FEATURE [PartDesign::Body] Body003  label="Lower Extrusion"
  Group = -> [Sketch008,Pad003,Sketch009,Pocket005,Local_CS005,Local_CS006,Local_CS007]
  Origin = -> Origin003
  Tip = -> Pocket005
COMPONENT P4 — geometry summary ("NEMA17"; no construction recipe available for this part):
  bounding box: 55.3 x 42.3 x 42.3 mm
  tessellated surface: 13,432 triangles
  volume: 42580 mm^3 (43% of its bounding box)
  symmetry: 4-fold rotationally symmetric about the z axis
COMPONENT P5 — recipe-attached ("TimingPulley", modeled in this document).
Construction recipe (the document's own serialized feature program — sketch geometry with constraints, then the solid features built on it; lengths are millimeters unless a unit is written):

FEATURE [Sketcher::SketchObject] Sketch015
  FullyConstrained = true
  MapMode = 5
  Support = -> [XY_Plane006]
  sketch-geometry (1):
    g0: Circle CenterX=0 CenterY=0 CenterZ=0 NormalX=0 NormalY=0 NormalZ=1 AngleXU=0 Radius=7.62
  constraints (2):
    c: Coincident(g0,g-1)
    c: Diameter(g0) = 15.24
FEATURE [PartDesign::Pad] Pad005
  Direction = (0,0,1)
  Length = 15.24
  Length2 = 10
  Profile = -> Sketch015
  ReferenceAxis = -> Sketch015 [N_Axis]
  Type = 0
FEATURE [PartDesign::Plane] DatumPlane001
  AttachmentOffset = pos=(0,0,-1.27) rot=(0,0,1;0rad)
  Length = 60
  MapMode = 5
  Placement = pos=(0,0,13.97) rot=(0,0,1;0rad)
  ResizeMode = 0
  Support = -> [Pad005]
  Width = 60
FEATURE [Sketcher::SketchObject] Sketch016
  ExternalGeometry = -> [Pad005]
  FullyConstrained = true
  MapMode = 5
  Placement = pos=(0,0,13.97) rot=(0,0,1;0rad)
  Support = -> [DatumPlane001]
  sketch-geometry (18):
    g0: ArcOfCircle CenterX=0 CenterY=7.62 CenterZ=0 NormalX=0 NormalY=0 NormalZ=1 AngleXU=0 Radius=1.27 StartAngle=3.22502 EndAngle=6.19976
    g1: ArcOfCircle CenterX=0 CenterY=0 CenterZ=0 NormalX=0 NormalY=0 NormalZ=1 AngleXU=0 Radius=7.62 StartAngle=1.40394 EndAngle=1.73766
    g2: ArcOfCircle CenterX=7.62 CenterY=0 CenterZ=0 NormalX=0 NormalY=0 NormalZ=1 AngleXU=0 Radius=1.27 StartAngle=1.65423 EndAngle=4.62896
    g3: ArcOfCircle CenterX=0 CenterY=-7.62 CenterZ=0 NormalX=0 NormalY=0 NormalZ=1 AngleXU=0 Radius=1.27 StartAngle=0.0834301 EndAngle=3.05816
    g4: ArcOfCircle CenterX=-7.62 CenterY=0 CenterZ=0 NormalX=0 NormalY=0 NormalZ=1 AngleXU=0 Radius=1.27 StartAngle=4.79582 EndAngle=7.77055
    g5: ArcOfCircle CenterX=-5.38815 CenterY=5.38815 CenterZ=0 NormalX=0 NormalY=0 NormalZ=1 AngleXU=0 Radius=1.27 StartAngle=4.01042 EndAngle=6.98515
    g6: ArcOfCircle CenterX=5.38815 CenterY=5.38815 CenterZ=0 NormalX=0 NormalY=0 NormalZ=1 AngleXU=0 Radius=1.27 StartAngle=2.43962 EndAngle=5.41436
    g7: ArcOfCircle CenterX=5.38815 CenterY=-5.38815 CenterZ=0 NormalX=0 NormalY=0 NormalZ=1 AngleXU=0 Radius=1.27 StartAngle=0.868828 EndAngle=3.84356
    g8: ArcOfCircle CenterX=-5.38815 CenterY=-5.38815 CenterZ=0 NormalX=0 NormalY=0 NormalZ=1 AngleXU=0 Radius=1.27 StartAngle=5.58122 EndAngle=8.55595
    g9: ArcOfCircle CenterX=0 CenterY=0 CenterZ=0 NormalX=0 NormalY=0 NormalZ=1 AngleXU=0 Radius=7.62 StartAngle=2.18933 EndAngle=2.52305
    g10: ArcOfCircle CenterX=0 CenterY=0 CenterZ=0 NormalX=0 NormalY=0 NormalZ=1 AngleXU=0 Radius=7.62 StartAngle=2.97473 EndAngle=3.30845
    g11: ArcOfCircle CenterX=0 CenterY=0 CenterZ=0 NormalX=0 NormalY=0 NormalZ=1 AngleXU=0 Radius=7.62 StartAngle=3.76013 EndAngle=4.09385
    g12: ArcOfCircle CenterX=0 CenterY=0 CenterZ=0 NormalX=0 NormalY=0 NormalZ=1 AngleXU=0 Radius=7.62 StartAngle=6.11633 EndAngle=6.45005
    g13: ArcOfCircle CenterX=0 CenterY=0 CenterZ=0 NormalX=0 NormalY=0 NormalZ=1 AngleXU=0 Radius=7.62 StartAngle=5.33093 EndAngle=5.66465
    g14: ArcOfCircle CenterX=0 CenterY=0 CenterZ=0 NormalX=0 NormalY=0 NormalZ=1 AngleXU=0 Radius=7.62 StartAngle=0.618538 EndAngle=0.952258
    g15: LineSegment StartX=5.38815 StartY=5.38815 StartZ=0 EndX=-5.38815 EndY=-5.38815 EndZ=0
    g16: LineSegment StartX=5.38815 StartY=-5.38815 StartZ=0 EndX=-5.38815 EndY=5.38815 EndZ=0
    g17: ArcOfCircle CenterX=-1.7e-15 CenterY=3.72e-14 CenterZ=0 NormalX=0 NormalY=0 NormalZ=1 AngleXU=0 Radius=7.62 StartAngle=4.54553 EndAngle=4.87925
  constraints (61):
    c: PointOnObject(g0,g-3)
    c: PointOnObject(g0,g-3)
    c: Radius(g0) = 1.27
    c: Coincident(g1,g-3)
    c: Coincident(g1,g0)
    c: Coincident(g1,g0)
    c: PointOnObject(g0,g-2)
    c: PointOnObject(g2,g-3)
    c: PointOnObject(g2,g-3)
    c: PointOnObject(g3,g-3)
    c: PointOnObject(g3,g-3)
    c: PointOnObject(g3,g-3)
    c: PointOnObject(g4,g-3)
    c: PointOnObject(g4,g-3)
    c: PointOnObject(g5,g-3)
    c: PointOnObject(g5,g-3)
    c: PointOnObject(g6,g-3)
    c: PointOnObject(g6,g-3)
    c: PointOnObject(g7,g-3)
    c: PointOnObject(g7,g-3)
    c: PointOnObject(g8,g-3)
    c: PointOnObject(g8,g-3)
    c: Coincident(g9,g1)
    c: Coincident(g9,g5)
    c: Coincident(g9,g5)
    c: Coincident(g10,g1)
    c: Coincident(g10,g4)
    c: Coincident(g10,g4)
    c: Coincident(g11,g1)
    c: Coincident(g11,g8)
    c: Coincident(g11,g8)
    c: Coincident(g12,g1)
    c: Coincident(g12,g2)
    c: Coincident(g12,g2)
    c: Coincident(g13,g1)
    c: Coincident(g13,g7)
    c: Coincident(g13,g7)
    c: Coincident(g14,g1)
    c: Coincident(g14,g6)
    c: Coincident(g14,g6)
    c: Equal(g0,g6)
    c: Equal(g6,g2)
    c: Equal(g2,g7)
    c: Equal(g7,g3)
    c: Equal(g3,g8)
    c: Equal(g8,g4)
    c: Equal(g4,g5)
    c: PointOnObject(g4,g-1)
    c: PointOnObject(g3,g-2)
    c: PointOnObject(g2,g-1)
    c: Coincident(g15,g6)
    c: Coincident(g15,g8)
    c: Coincident(g16,g7)
    c: Coincident(g16,g5)
    c: PointOnObject(g1,g15)
    c: PointOnObject(g1,g16)
    c: Perpendicular(g16,g15)
    c: Angle(g15,g-2) = 0.785398
    c: Coincident(g17,g3)
    c: Coincident(g17,g3)
    c: Equal(g17,g13)
FEATURE [PartDesign::Pocket] Pocket010
  BaseFeature = -> Pad005
  Direction = (0,0,-1)
  Length = 12.7
  Length2 = 5
  Profile = -> Sketch016
  ReferenceAxis = -> Sketch016 [N_Axis]
  Type = 0
FEATURE [Sketcher::SketchObject] Sketch017
  FullyConstrained = true
  MapMode = 5
  Placement = pos=(0,0,15.24) rot=(0,0,1;0rad)
  Support = -> [Pocket010]
  sketch-geometry (1):
    g0: Circle CenterX=0 CenterY=0 CenterZ=0 NormalX=0 NormalY=0 NormalZ=1 AngleXU=0 Radius=2.54
  constraints (2):
    c: Coincident(g0,g-1)
    c: Diameter(g0) = 5.08
FEATURE [PartDesign::Pocket] Pocket011
  BaseFeature = -> Pocket010
  Direction = (0,0,-1)
  Length = 5
  Length2 = 5
  Profile = -> Sketch017
  ReferenceAxis = -> Sketch017 [N_Axis]
  Type = 1
FEATURE [PartDesign::CoordinateSystem] Local_CS009  label="MotorShaftMount"
  AttacherType = Attacher::AttachEngine3D
  MapMode = 11
  Placement = pos=(0,0,15.24) rot=(0,0,1;1.5708rad)
  Support = -> [Pocket011]
FEATURE [PartDesign::Body] Body005  label="TimingPulley"
  Group = -> [Sketch015,Pad005,DatumPlane001,Sketch016,Pocket010,Sketch017,Pocket011,Local_CS009]
  Origin = -> Origin006
  Tip = -> Pocket011
COMPONENT P6 — recipe-attached ("Rail", modeled in this document).
Construction recipe (the document's own serialized feature program — sketch geometry with constraints, then the solid features built on it; lengths are millimeters unless a unit is written):

FEATURE [Sketcher::SketchObject] Sketch018
  FullyConstrained = true
  MapMode = 5
  Placement = pos=(0,0,0) rot=(0.57735,0.57735,0.57735;2.0944rad)
  Support = -> [YZ_Plane007]
  sketch-geometry (1):
    g0: Circle CenterX=0 CenterY=0 CenterZ=0 NormalX=0 NormalY=0 NormalZ=1 AngleXU=0 Radius=4
  constraints (2):
    c: Coincident(g0,g-1)
    c: Diameter(g0) = 8
FEATURE [PartDesign::Pad] Pad006
  Direction = (1,-2e-16,3e-16)
  Length = 914.4
  Length2 = 10
  Midplane = true
  Placement = pos=(0,0,0) rot=(0.57735,0.57735,0.57735;2.0944rad)
  Profile = -> Sketch018
  ReferenceAxis = -> Sketch018 [N_Axis]
  Type = 0
FEATURE [PartDesign::CoordinateSystem] Local_CS013  label="Mount"
  AttacherType = Attacher::AttachEngine3D
  MapMode = 11
  Placement = pos=(-457.2,2.034e-13,-1.27e-13) rot=(0.707107,0,0.707107;3.14159rad)
  Support = -> [Pad006]
FEATURE [PartDesign::Body] Body006  label="Rail"
  Group = -> [Sketch018,Pad006,Local_CS013]
  Origin = -> Origin007
  Tip = -> Pad006
COMPONENT P7 — recipe-attached ("Eccentric", modeled in this document).
Construction recipe (the document's own serialized feature program — sketch geometry with constraints, then the solid features built on it; lengths are millimeters unless a unit is written):

FEATURE [Sketcher::SketchObject] Sketch019
  FullyConstrained = true
  MapMode = 5
  Placement = pos=(0,0,0) rot=(1,0,0;1.5708rad)
  Support = -> [XZ_Plane008]
  sketch-geometry (2):
    g0: Circle CenterX=0 CenterY=0 CenterZ=0 NormalX=0 NormalY=0 NormalZ=1 AngleXU=0 Radius=2.5
    g1: Circle CenterX=-0.762 CenterY=0 CenterZ=0 NormalX=0 NormalY=0 NormalZ=1 AngleXU=0 Radius=3.5
  constraints (5):
    c: Coincident(g0,g-1)
    c: PointOnObject(g1,g-1)
    c: Diameter(g0) = 5
    c: Diameter(g1) = 7
    c: Distance(g1,g0) = 0.762
FEATURE [PartDesign::Pad] Pad007
  Direction = (0,-1,2e-16)
  Length = 12.7
  Length2 = 10
  Placement = pos=(0,0,0) rot=(1,0,0;1.5708rad)
  Profile = -> Sketch019
  ReferenceAxis = -> Sketch019 [N_Axis]
  Type = 0
FEATURE [PartDesign::CoordinateSystem] Local_CS014
  AttacherType = Attacher::AttachEngine3D
  MapMode = 11
  Placement = pos=(0,0,0) rot=(0.57735,-0.57735,0.57735;2.0944rad)
  Support = -> [Pad007]
FEATURE [PartDesign::Body] Body007  label="Eccentric"
  Group = -> [Sketch019,Pad007,Local_CS014]
  Origin = -> Origin008
  Tip = -> Pad007
COMPONENT P8 — recipe-attached ("Endplate", modeled in this document).
Construction recipe (the document's own serialized feature program — sketch geometry with constraints, then the solid features built on it; lengths are millimeters unless a unit is written):

FEATURE [Sketcher::SketchObject] Sketch022
  FullyConstrained = true
  MapMode = 5
  Placement = pos=(0,0,0) rot=(0.57735,0.57735,0.57735;2.0944rad)
  Support = -> [YZ_Plane009]
  sketch-geometry (4):
    g0: LineSegment StartX=-73.025 StartY=0 StartZ=0 EndX=73.025 EndY=0 EndZ=0
    g1: LineSegment StartX=73.025 StartY=0 StartZ=0 EndX=50.8 EndY=80.9625 EndZ=0
    g2: LineSegment StartX=50.8 StartY=80.9625 StartZ=0 EndX=-50.8 EndY=80.9625 EndZ=0
    g3: LineSegment StartX=-50.8 StartY=80.9625 StartZ=0 EndX=-73.025 EndY=0 EndZ=0
  constraints (10):
    c: PointOnObject(g0,g-1)
    c: Coincident(g1,g0)
    c: Coincident(g2,g1)
    c: Coincident(g3,g2)
    c: Coincident(g3,g0)
    c: Symmetric(g0,g0,g-2)
    c: Symmetric(g1,g2,g-2)
    c: Distance(g1,g0) = 80.9625
    c: Distance(g2) = 101.6
    c: Distance(g0) = 146.05
FEATURE [PartDesign::Pad] Pad008
  Direction = (1,-2e-16,3e-16)
  Length = 4
  Length2 = 10
  Placement = pos=(0,0,0) rot=(0.57735,0.57735,0.57735;2.0944rad)
  Profile = -> Sketch022
  ReferenceAxis = -> Sketch022 [N_Axis]
  Type = 0
FEATURE [Sketcher::SketchObject] Sketch026
  ExternalGeometry = -> [Pad008]
  FullyConstrained = true
  MapMode = 5
  Placement = pos=(4,-9e-16,9e-16) rot=(0.57735,0.57735,0.57735;2.0944rad)
  Support = -> [Pad008]
  sketch-geometry (2):
    g0: Circle CenterX=0 CenterY=61.1378 CenterZ=0 NormalX=0 NormalY=0 NormalZ=1 AngleXU=0 Radius=3.175
    g1: Circle CenterX=0 CenterY=23.0378 CenterZ=0 NormalX=0 NormalY=0 NormalZ=1 AngleXU=0 Radius=3.175
  constraints (6):
    c: PointOnObject(g0,g-2)
    c: PointOnObject(g1,g-2)
    c: Equal(g1,g0)
    c: Diameter(g0) = 6.35
    c: Distance(g0,g1) = 38.1
    c: Distance(g0,g-3) = 19.8247
FEATURE [PartDesign::Pocket] Pocket014
  BaseFeature = -> Pad008
  Direction = (-1,4e-16,-4e-16)
  Length = 5.0038
  Length2 = 5
  Placement = pos=(0,0,0) rot=(0.57735,0.57735,0.57735;2.0944rad)
  Profile = -> Sketch026
  ReferenceAxis = -> Sketch026 [N_Axis]
  Type = 0
FEATURE [PartDesign::Body] Body008  label="Endplate"
  Group = -> [Sketch022,Pad008,Sketch026,Pocket014]
  Origin = -> Origin009
  Placement = pos=(457.342,0,-3.95554) rot=(0,0,1;0rad)
  Tip = -> Pocket014
COMPONENT P9 — recipe-attached ("BottomPanel", modeled in this document).
Construction recipe (the document's own serialized feature program — sketch geometry with constraints, then the solid features built on it; lengths are millimeters unless a unit is written):

FEATURE [Sketcher::SketchObject] Sketch023
  FullyConstrained = true
  MapMode = 5
  Support = -> [XY_Plane010]
  sketch-geometry (5):
    g0: LineSegment StartX=-431.8 StartY=73.025 StartZ=0 EndX=-431.8 EndY=-73.025 EndZ=0
    g1: LineSegment StartX=-431.8 StartY=-73.025 StartZ=0 EndX=431.8 EndY=-73.025 EndZ=0
    g2: LineSegment StartX=431.8 StartY=-73.025 StartZ=0 EndX=431.8 EndY=73.025 EndZ=0
    g3: LineSegment StartX=431.8 StartY=73.025 StartZ=0 EndX=-431.8 EndY=73.025 EndZ=0
    g4: GeomPoint X=0 Y=0 Z=0
  constraints (12):
    c: Coincident(g0,g1)
    c: Coincident(g1,g2)
    c: Coincident(g2,g3)
    c: Coincident(g3,g0)
    c: Horizontal(g1)
    c: Horizontal(g3)
    c: Vertical(g0)
    c: Vertical(g2)
    c: Symmetric(g1,g0,g4)
    c: Coincident(g4,g-1)
    c: Distance(g2) = 146.05
    c: Distance(g1) = 863.6
FEATURE [PartDesign::Pad] Pad009
  Direction = (0,0,1)
  Length = 3.9878
  Length2 = 10
  Profile = -> Sketch023
  ReferenceAxis = -> Sketch023 [N_Axis]
  Reversed = true
  Type = 0
FEATURE [Sketcher::SketchObject] Sketch027
  FullyConstrained = true
  MapMode = 5
  Placement = pos=(0,0,-3.9878) rot=(1,0,0;3.14159rad)
  Support = -> [Pad009]
  sketch-geometry (5):
    g0: LineSegment StartX=0 StartY=0 StartZ=0 EndX=-355.6 EndY=0 EndZ=0
    g1: LineSegment StartX=0 StartY=0 StartZ=0 EndX=355.6 EndY=0 EndZ=0
    g2: Circle CenterX=-355.6 CenterY=0 CenterZ=0 NormalX=0 NormalY=0 NormalZ=1 AngleXU=0 Radius=3.175
    g3: Circle CenterX=0 CenterY=0 CenterZ=0 NormalX=0 NormalY=0 NormalZ=1 AngleXU=0 Radius=3.175
    g4: Circle CenterX=355.6 CenterY=0 CenterZ=0 NormalX=0 NormalY=0 NormalZ=1 AngleXU=0 Radius=3.175
  constraints (12):
    c: Coincident(g0,g-1)
    c: Horizontal(g0)
    c: Coincident(g1,g0)
    c: PointOnObject(g1,g-1)
    c: Equal(g1,g0)
    c: Coincident(g2,g0)
    c: Coincident(g3,g0)
    c: Coincident(g4,g1)
    c: Equal(g4,g3)
    c: Equal(g3,g2)
    c: Diameter(g2) = 6.35
    c: Distance(g0) = 355.6
FEATURE [PartDesign::Pocket] Pocket015
  BaseFeature = -> Pad009
  Direction = (0,0,1)
  Length = 5
  Length2 = 5
  Profile = -> Sketch027
  ReferenceAxis = -> Sketch027 [N_Axis]
  Type = 1
FEATURE [PartDesign::Body] Body009  label="BottomPanel"
  Group = -> [Sketch023,Pad009,Sketch027,Pocket015]
  Origin = -> Origin010
  Tip = -> Pocket015
COMPONENT P10 — recipe-attached ("TopPanel", modeled in this document).
Construction recipe (the document's own serialized feature program — sketch geometry with constraints, then the solid features built on it; lengths are millimeters unless a unit is written):

FEATURE [Sketcher::SketchObject] Sketch024
  FullyConstrained = true
  MapMode = 5
  Support = -> [XY_Plane011]
  sketch-geometry (13):
    g0: LineSegment StartX=-457.2 StartY=50.8 StartZ=0 EndX=457.2 EndY=50.8 EndZ=0
    g1: LineSegment StartX=457.2 StartY=-50.8 StartZ=0 EndX=-457.2 EndY=-50.8 EndZ=0
    g2: GeomPoint X=0 Y=-1e-16 Z=0
    g3: LineSegment StartX=457.2 StartY=50.8 StartZ=0 EndX=457.2 EndY=12.7 EndZ=0
    g4: LineSegment StartX=457.2 StartY=12.7 StartZ=0 EndX=431.8 EndY=12.7 EndZ=0
    g5: LineSegment StartX=431.8 StartY=12.7 StartZ=0 EndX=431.8 EndY=-12.7 EndZ=0
    g6: LineSegment StartX=431.8 StartY=-12.7 StartZ=0 EndX=457.2 EndY=-12.7 EndZ=0
    g7: LineSegment StartX=457.2 StartY=-12.7 StartZ=0 EndX=457.2 EndY=-50.8 EndZ=0
    g8: LineSegment StartX=-457.2 StartY=50.8 StartZ=0 EndX=-457.2 EndY=12.7 EndZ=0
    g9: LineSegment StartX=-457.2 StartY=12.7 StartZ=0 EndX=-431.8 EndY=12.7 EndZ=0
    g10: LineSegment StartX=-431.8 StartY=12.7 StartZ=0 EndX=-431.8 EndY=-12.7 EndZ=0
    g11: LineSegment StartX=-431.8 StartY=-12.7 StartZ=0 EndX=-457.2 EndY=-12.7 EndZ=0
    g12: LineSegment StartX=-457.2 StartY=-12.7 StartZ=0 EndX=-457.2 EndY=-50.8 EndZ=0
  constraints (34):
    c: Horizontal(g0)
    c: Horizontal(g1)
    c: Symmetric(g0,g1,g2)
    c: Coincident(g2,g-1)
    c: Distance(g0) = 914.4
    c: Coincident(g3,g0)
    c: Vertical(g3)
    c: Coincident(g4,g3)
    c: Horizontal(g4)
    c: Coincident(g5,g4)
    c: Vertical(g5)
    c: Coincident(g6,g5)
    c: Horizontal(g6)
    c: Coincident(g7,g6)
    c: Coincident(g7,g1)
    c: Coincident(g8,g0)
    c: Vertical(g8)
    c: Coincident(g9,g8)
    c: Horizontal(g9)
    c: Coincident(g10,g9)
    c: Vertical(g10)
    c: Coincident(g11,g10)
    c: Horizontal(g11)
    c: Coincident(g12,g11)
    c: Coincident(g12,g1)
    c: Tangent(g12,g8)
    c: Tangent(g3,g7)
    c: Equal(g4,g5)
    c: Equal(g6,g9)
    c: Equal(g9,g10)
    c: Equal(g12,g8)
    c: Equal(g8,g3)
    c: Distance(g4) = 25.4
    c: Distance(g0,g1) = 101.6
FEATURE [PartDesign::Pad] Pad010
  Direction = (0,0,1)
  Length = 4
  Length2 = 10
  Profile = -> Sketch024
  ReferenceAxis = -> Sketch024 [N_Axis]
  Type = 0
FEATURE [PartDesign::Body] Body010  label="TopPanel"
  Group = -> [Sketch024,Pad010]
  Origin = -> Origin011
  Placement = pos=(0,0,72.7001) rot=(0,0,1;0rad)
  Tip = -> Pad010
COMPONENT P11 — recipe-attached ("FacePanel", modeled in this document).
Construction recipe (the document's own serialized feature program — sketch geometry with constraints, then the solid features built on it; lengths are millimeters unless a unit is written):

FEATURE [Sketcher::SketchObject] Sketch025
  FullyConstrained = true
  MapMode = 5
  Placement = pos=(0,0,0) rot=(1,0,0;1.5708rad)
  Support = -> [XZ_Plane012]
  sketch-geometry (5):
    g0: LineSegment StartX=-461.2 StartY=-36.576 StartZ=0 EndX=-461.2 EndY=36.576 EndZ=0
    g1: LineSegment StartX=-461.2 StartY=36.576 StartZ=0 EndX=461.2 EndY=36.576 EndZ=0
    g2: LineSegment StartX=461.2 StartY=36.576 StartZ=0 EndX=461.2 EndY=-36.576 EndZ=0
    g3: LineSegment StartX=461.2 StartY=-36.576 StartZ=0 EndX=-461.2 EndY=-36.576 EndZ=0
    g4: GeomPoint X=0 Y=0 Z=0
  constraints (12):
    c: Coincident(g0,g1)
    c: Coincident(g1,g2)
    c: Coincident(g2,g3)
    c: Coincident(g3,g0)
    c: Horizontal(g1)
    c: Horizontal(g3)
    c: Vertical(g0)
    c: Vertical(g2)
    c: Symmetric(g1,g0,g4)
    c: Coincident(g4,g-1)
    c: Distance(g1) = 922.4
    c: Distance(g0) = 73.152
FEATURE [PartDesign::Pad] Pad011
  Direction = (0,-1,2e-16)
  Length = 4
  Length2 = 10
  Placement = pos=(0,0,0) rot=(1,0,0;1.5708rad)
  Profile = -> Sketch025
  ReferenceAxis = -> Sketch025 [N_Axis]
  Type = 0
FEATURE [PartDesign::Body] Body011  label="FacePanel"
  Group = -> [Sketch025,Pad011]
  Origin = -> Origin012
  Placement = pos=(0,-62.0274,34.8655) rot=(-1,0,0;0.314159rad)
  Tip = -> Pad011
COMPONENT P12 — recipe-attached ("MotorSpacer", modeled in this document).
Construction recipe (the document's own serialized feature program — sketch geometry with constraints, then the solid features built on it; lengths are millimeters unless a unit is written):

FEATURE [Sketcher::SketchObject] Sketch028
  FullyConstrained = true
  MapMode = 5
  Placement = pos=(0,0,0) rot=(1,0,0;1.5708rad)
  Support = -> [XZ_Plane013]
  sketch-geometry (15):
    g0: ArcOfCircle CenterX=3.175 CenterY=0 CenterZ=0 NormalX=0 NormalY=0 NormalZ=1 AngleXU=0 Radius=20.32 StartAngle=2.60295 EndAngle=3.68024
    g1: ArcOfCircle CenterX=-3.175 CenterY=0 CenterZ=0 NormalX=0 NormalY=0 NormalZ=1 AngleXU=0 Radius=20.32 StartAngle=5.74454 EndAngle=6.82183
    g2: ArcOfCircle CenterX=0 CenterY=21.9203 CenterZ=0 NormalX=0 NormalY=0 NormalZ=1 AngleXU=0 Radius=6.35 StartAngle=0.538647 EndAngle=2.60295
    g3: ArcOfCircle CenterX=0 CenterY=-21.9203 CenterZ=0 NormalX=0 NormalY=0 NormalZ=1 AngleXU=0 Radius=6.35 StartAngle=3.68024 EndAngle=5.74454
    g4: LineSegment StartX=0 StartY=21.9203 StartZ=0 EndX=-21.9203 EndY=0 EndZ=0
    g5: LineSegment StartX=-21.9203 StartY=0 StartZ=0 EndX=0 EndY=-21.9203 EndZ=0
    g6: LineSegment StartX=0 StartY=-21.9203 StartZ=0 EndX=21.9203 EndY=0 EndZ=0
    g7: LineSegment StartX=21.9203 StartY=0 StartZ=0 EndX=0 EndY=21.9203 EndZ=0
    g8: LineSegment StartX=-5.45086 StartY=25.1777 StartZ=0 EndX=-14.2678 EndY=10.4236 EndZ=0
    g9: LineSegment StartX=-14.2678 StartY=-10.4236 StartZ=0 EndX=-5.45086 EndY=-25.1777 EndZ=0
    g10: LineSegment StartX=5.45086 StartY=-25.1777 StartZ=0 EndX=14.2678 EndY=-10.4236 EndZ=0
    g11: LineSegment StartX=14.2678 StartY=10.4236 StartZ=0 EndX=5.45086 EndY=25.1777 EndZ=0
    g12: Circle CenterX=0 CenterY=21.9203 CenterZ=0 NormalX=0 NormalY=0 NormalZ=1 AngleXU=0 Radius=2.25
    g13: Circle CenterX=0 CenterY=-21.9203 CenterZ=0 NormalX=0 NormalY=0 NormalZ=1 AngleXU=0 Radius=2.25
    g14: Circle CenterX=0 CenterY=0 CenterZ=0 NormalX=0 NormalY=0 NormalZ=1 AngleXU=0 Radius=11.125
  constraints (35):
    c: PointOnObject(g0,g-1)
    c: PointOnObject(g2,g-2)
    c: PointOnObject(g3,g-2)
    c: Coincident(g4,g2)
    c: PointOnObject(g4,g-1)
    c: Coincident(g5,g4)
    c: Coincident(g5,g3)
    c: Coincident(g6,g3)
    c: Coincident(g7,g6)
    c: Coincident(g7,g2)
    c: Equal(g5,g4)
    c: Equal(g4,g7)
    c: Equal(g7,g6)
    c: Perpendicular(g6,g7)
    c: Distance(g4) = 31
    c: Tangent(g11,g2) = -1.5708
    c: Tangent(g8,g2) = -1.5708
    c: Tangent(g8,g0) = -1.5708
    c: Tangent(g9,g0) = -1.5708
    c: Tangent(g9,g3) = -1.5708
    c: Tangent(g10,g3) = -1.5708
    c: Tangent(g10,g1) = -1.5708
    c: Tangent(g11,g1) = -1.5708
    c: Symmetric(g1,g0,g-1)
    c: Coincident(g12,g2)
    c: Coincident(g13,g3)
    c: Equal(g13,g12)
    c: Diameter(g12) = 4.5
    c: Equal(g2,g3)
    c: Radius(g2) = 6.35
    c: Coincident(g14,g-1)
    c: Diameter(g14) = 22.25
    c: Equal(g1,g0)
    c: Radius(g0) = 20.32
    c: Distance(g1,g14) = 3.175
FEATURE [PartDesign::Pad] Pad012
  Direction = (0,-1,-2e-16)
  Length = 3.683
  Length2 = 10
  Placement = pos=(0,0,0) rot=(1,0,0;1.5708rad)
  Profile = -> Sketch028
  ReferenceAxis = -> Sketch028 [N_Axis]
  Type = 0
FEATURE [PartDesign::Body] Body012  label="MotorSpacer"
  Group = -> [Sketch028,Pad012]
  Origin = -> Origin013
  Tip = -> Pad012
COMPONENT P13 — recipe-attached ("EncoderHolder", modeled in this document).
Construction recipe (the document's own serialized feature program — sketch geometry with constraints, then the solid features built on it; lengths are millimeters unless a unit is written):

FEATURE [Sketcher::SketchObject] Sketch029
  FullyConstrained = true
  MapMode = 5
  Placement = pos=(0,0,0) rot=(1,0,0;1.5708rad)
  Support = -> [XZ_Plane014]
  sketch-geometry (14):
    g0: Circle CenterX=-12.7 CenterY=-7.33235 CenterZ=0 NormalX=0 NormalY=0 NormalZ=1 AngleXU=0 Radius=1.778
    g1: Circle CenterX=12.7 CenterY=-7.33235 CenterZ=0 NormalX=0 NormalY=0 NormalZ=1 AngleXU=0 Radius=1.778
    g2: Circle CenterX=0 CenterY=14.6647 CenterZ=0 NormalX=0 NormalY=0 NormalZ=1 AngleXU=0 Radius=1.778
    g3: ArcOfCircle CenterX=-3e-16 CenterY=1e-16 CenterZ=0 NormalX=0 NormalY=0 NormalZ=1 AngleXU=0 Radius=25 StartAngle=3.863e-13 EndAngle=3.14159
    g4: LineSegment StartX=25 StartY=9.6576e-12 StartZ=0 EndX=25 EndY=-25.4 EndZ=0
    g5: LineSegment StartX=25 StartY=-25.4 StartZ=0 EndX=-25 EndY=-25.4 EndZ=0
    g6: LineSegment StartX=-25 StartY=-25.4 StartZ=0 EndX=-25 EndY=-2.7818e-12 EndZ=0
    g7: LineSegment StartX=0 StartY=14.6647 StartZ=0 EndX=-12.7 EndY=-7.33235 EndZ=0
    g8: LineSegment StartX=-12.7 StartY=-7.33235 StartZ=0 EndX=12.7 EndY=-7.33235 EndZ=0
    g9: LineSegment StartX=12.7 StartY=-7.33235 StartZ=0 EndX=0 EndY=14.6647 EndZ=0
    g10: LineSegment StartX=-3e-16 StartY=1e-16 StartZ=0 EndX=-12.7 EndY=-7.33235 EndZ=0
    g11: LineSegment StartX=-3e-16 StartY=1e-16 StartZ=0 EndX=12.7 EndY=-7.33235 EndZ=0
    g12: LineSegment StartX=-3e-16 StartY=1e-16 StartZ=0 EndX=0 EndY=14.6647 EndZ=0
    g13: Circle CenterX=-3e-16 CenterY=1e-16 CenterZ=0 NormalX=0 NormalY=0 NormalZ=1 AngleXU=0 Radius=10.287
  constraints (35):
    c: PointOnObject(g2,g-2)
    c: Coincident(g3,g-1)
    c: PointOnObject(g3,g-1)
    c: PointOnObject(g3,g-1)
    c: Coincident(g4,g3)
    c: Vertical(g4)
    c: Coincident(g5,g4)
    c: Horizontal(g5)
    c: Coincident(g6,g5)
    c: Coincident(g6,g3)
    c: Vertical(g6)
    c: Equal(g2,g0)
    c: Equal(g0,g1)
    c: Coincident(g7,g2)
    c: Coincident(g7,g0)
    c: Coincident(g8,g0)
    c: Coincident(g8,g1)
    c: Coincident(g9,g1)
    c: Coincident(g9,g2)
    c: Horizontal(g8)
    c: Equal(g7,g9)
    c: Equal(g9,g8)
    c: Distance(g8) = 25.4
    c: Diameter(g2) = 3.556
    c: Coincident(g10,g3)
    c: Coincident(g10,g0)
    c: Coincident(g11,g3)
    c: Coincident(g11,g1)
    c: Coincident(g12,g3)
    c: Coincident(g12,g2)
    c: Equal(g12,g10)
    c: Radius(g3) = 25
    c: Distance(g4) = 25.4
    c: Coincident(g13,g3)
    c: Diameter(g13) = 20.574
FEATURE [PartDesign::Pad] Pad013
  Direction = (0,-1,-2e-16)
  Length = 5.08
  Length2 = 10
  Placement = pos=(0,0,0) rot=(1,0,0;1.5708rad)
  Profile = -> Sketch029
  ReferenceAxis = -> Sketch029 [N_Axis]
  Type = 0
FEATURE [Sketcher::SketchObject] Sketch030
  ExternalGeometry = -> [Pad013]
  FullyConstrained = true
  MapMode = 5
  Placement = pos=(0,0,0) rot=(-1,0,0;1.5708rad)
  Support = -> [Pad013]
  sketch-geometry (6):
    g0: ArcOfCircle CenterX=0 CenterY=0 CenterZ=0 NormalX=0 NormalY=0 NormalZ=1 AngleXU=0 Radius=20.32 StartAngle=3e-16 EndAngle=3.14159
    g1: LineSegment StartX=-20.32 StartY=-2.141e-13 StartZ=0 EndX=-25 EndY=0 EndZ=0
    g2: LineSegment StartX=-25 StartY=0 StartZ=0 EndX=-25 EndY=25.4 EndZ=0
    g3: LineSegment StartX=-25 StartY=25.4 StartZ=0 EndX=25 EndY=25.4 EndZ=0
    g4: LineSegment StartX=25 StartY=25.4 StartZ=0 EndX=25 EndY=0 EndZ=0
    g5: LineSegment StartX=25 StartY=0 StartZ=0 EndX=20.32 EndY=5.9e-15 EndZ=0
  constraints (16):
    c: Coincident(g0,g-1)
    c: PointOnObject(g0,g-1)
    c: PointOnObject(g0,g-1)
    c: Radius(g0) = 20.32
    c: Coincident(g1,g0)
    c: PointOnObject(g1,g-1)
    c: Coincident(g2,g1)
    c: Coincident(g2,g-4)
    c: Vertical(g2)
    c: Coincident(g3,g2)
    c: Coincident(g3,g-3)
    c: Coincident(g4,g3)
    c: PointOnObject(g4,g-1)
    c: Vertical(g4)
    c: Coincident(g5,g4)
    c: Coincident(g5,g0)
FEATURE [PartDesign::Pad] Pad014
  BaseFeature = -> Pad013
  Direction = (0,1,2e-16)
  Length = 40.64
  Length2 = 10
  Placement = pos=(0,0,0) rot=(1,0,0;1.5708rad)
  Profile = -> Sketch030
  ReferenceAxis = -> Sketch030 [N_Axis]
  Type = 0
FEATURE [Sketcher::SketchObject] Sketch031
  ExternalGeometry = -> [Pad014]
  FullyConstrained = true
  MapMode = 5
  Placement = pos=(0,0,1.1437e-12) rot=(0,0,1;3.14159rad)
  Support = -> [Pad014]
  sketch-geometry (8):
    g0: LineSegment StartX=-18 StartY=-1.27 StartZ=0 EndX=18 EndY=-1.27 EndZ=0
    g1: LineSegment StartX=18 StartY=-1.27 StartZ=0 EndX=18 EndY=-34.29 EndZ=0
    g2: LineSegment StartX=18 StartY=-34.29 StartZ=0 EndX=-18 EndY=-34.29 EndZ=0
    g3: LineSegment StartX=-18 StartY=-34.29 StartZ=0 EndX=-18 EndY=-1.27 EndZ=0
    g4: Circle CenterX=-18 CenterY=-1.27 CenterZ=0 NormalX=0 NormalY=0 NormalZ=1 AngleXU=0 Radius=1.27
    g5: Circle CenterX=18 CenterY=-1.27 CenterZ=0 NormalX=0 NormalY=0 NormalZ=1 AngleXU=0 Radius=1.27
    g6: Circle CenterX=18 CenterY=-34.29 CenterZ=0 NormalX=0 NormalY=0 NormalZ=1 AngleXU=0 Radius=1.27
    g7: Circle CenterX=-18 CenterY=-34.29 CenterZ=0 NormalX=0 NormalY=0 NormalZ=1 AngleXU=0 Radius=1.27
  constraints (19):
    c: Coincident(g0,g1)
    c: Coincident(g1,g2)
    c: Coincident(g2,g3)
    c: Coincident(g3,g0)
    c: Horizontal(g2)
    c: Vertical(g1)
    c: Vertical(g3)
    c: Symmetric(g0,g0,g-2)
    c: Coincident(g4,g0)
    c: Coincident(g5,g0)
    c: Coincident(g6,g1)
    c: Coincident(g7,g2)
    c: Equal(g7,g4)
    c: Equal(g4,g5)
    c: Equal(g5,g6)
    c: Diameter(g5) = 2.54
    c: Distance(g5,g-3) = 6.35
    c: Distance(g1) = 33.02
    c: Distance(g2) = 36
FEATURE [PartDesign::Hole] Hole
  BaseFeature = -> Pad014
  CustomThreadClearance = 0
  Depth = 170.573
  DepthType = 1
  Diameter = 3.5052
  DrillForDepth = false
  DrillPoint = 1
  DrillPointAngle = 118
  HoleCutCountersinkAngle = 90
  HoleCutCustomValues = false
  HoleCutDepth = 19.05
  HoleCutDiameter = 6.4008
  HoleCutType = 1
  ModelThread = false
  Placement = pos=(0,0,0) rot=(1,0,0;1.5708rad)
  Profile = -> Sketch031
  Tapered = false
  TaperedAngle = 90
  ThreadClass = 0
  ThreadDepth = 170.573
  ThreadDepthType = 0
  ThreadDirection = 0
  ThreadFit = 0
  ThreadSize = 0
  ThreadType = 0
  Threaded = false
  UseCustomThreadClearance = false
FEATURE [Sketcher::SketchObject] Sketch035
  ExternalGeometry = -> [Hole]
  FullyConstrained = true
  MapMode = 5
  Placement = pos=(0,40.64,9e-15) rot=(-1,0,0;1.5708rad)
  Support = -> [Hole]
  sketch-geometry (5):
    g0: LineSegment StartX=0 StartY=0 StartZ=0 EndX=25 EndY=14.4338 EndZ=0
    g1: LineSegment StartX=25 StartY=14.4338 StartZ=0 EndX=25 EndY=0 EndZ=0
    g2: LineSegment StartX=25 StartY=0 StartZ=0 EndX=-25 EndY=0 EndZ=0
    g3: LineSegment StartX=-25 StartY=0 StartZ=0 EndX=-25 EndY=14.4338 EndZ=0
    g4: LineSegment StartX=-25 StartY=14.4338 StartZ=0 EndX=0 EndY=0 EndZ=0
  constraints (14):
    c: Coincident(g0,g-1)
    c: Coincident(g1,g0)
    c: PointOnObject(g1,g-1)
    c: Vertical(g1)
    c: Coincident(g2,g1)
    c: Horizontal(g2)
    c: Coincident(g3,g2)
    c: Coincident(g4,g3)
    c: Coincident(g4,g0)
    c: Vertical(g3)
    c: Equal(g4,g0)
    c: Equal(g3,g1)
    c: PointOnObject(g3,g-3)
    c: Angle(g2,g4) = 2.61799
FEATURE [PartDesign::Pocket] Pocket017
  BaseFeature = -> Hole
  Direction = (0,-1,-2e-16)
  Length = 15.24
  Length2 = 5
  Placement = pos=(0,0,0) rot=(1,0,0;1.5708rad)
  Profile = -> Sketch035
  ReferenceAxis = -> Sketch035 [N_Axis]
  Type = 0
FEATURE [Sketcher::SketchObject] Sketch036
  ExternalGeometry = -> [Pocket017]
  FullyConstrained = true
  MapMode = 5
  Placement = pos=(0,-5.08,-1.1e-15) rot=(1,0,0;1.5708rad)
  Support = -> [Pocket017]
  sketch-geometry (3):
    g0: Circle CenterX=12.7 CenterY=-7.33235 CenterZ=0 NormalX=0 NormalY=0 NormalZ=1 AngleXU=0 Radius=2.921
    g1: Circle CenterX=0 CenterY=14.6647 CenterZ=0 NormalX=0 NormalY=0 NormalZ=1 AngleXU=0 Radius=2.921
    g2: Circle CenterX=-12.7 CenterY=-7.33235 CenterZ=0 NormalX=0 NormalY=0 NormalZ=1 AngleXU=0 Radius=2.921
  constraints (6):
    c: Coincident(g0,g-3)
    c: Coincident(g1,g-4)
    c: Coincident(g2,g-5)
    c: Equal(g2,g0)
    c: Equal(g0,g1)
    c: Diameter(g1) = 5.842
FEATURE [PartDesign::Pocket] Pocket018
  BaseFeature = -> Pocket017
  Direction = (0,1,2e-16)
  Length = 1.778
  Length2 = 5
  Placement = pos=(0,0,0) rot=(1,0,0;1.5708rad)
  Profile = -> Sketch036
  ReferenceAxis = -> Sketch036 [N_Axis]
  Type = 0
FEATURE [PartDesign::Fillet] Fillet
  Base = -> Pocket018 [Edge61,Edge59,Edge54,Edge57]
  BaseFeature = -> Pocket018
  Placement = pos=(0,0,0) rot=(1,0,0;1.5708rad)
  Radius = 1.524
  SupportTransform = false
  UseAllEdges = false
FEATURE [PartDesign::Fillet] Fillet001
  Base = -> Fillet [Edge66,Edge28]
  BaseFeature = -> Fillet
  Placement = pos=(0,0,0) rot=(1,0,0;1.5708rad)
  Radius = 5.08
  SupportTransform = false
  UseAllEdges = false
FEATURE [PartDesign::Chamfer] Chamfer
  Angle = 45
  Base = -> Fillet001 [Edge119,Edge118,Edge117]
  BaseFeature = -> Fillet001
  ChamferType = 0
  FlipDirection = false
  Placement = pos=(0,0,0) rot=(1,0,0;1.5708rad)
  Size = 0.508
  Size2 = 1
  SupportTransform = false
  UseAllEdges = false
FEATURE [PartDesign::Body] Body013  label="EncoderHolder"
  Group = -> [Sketch029,Pad013,Sketch030,Pad014,Sketch031,Hole,Sketch035,Pocket017,Sketch036,Pocket018,Fillet,Fillet001,Chamfer]
  Origin = -> Origin014
  Tip = -> Chamfer
COMPONENT P14 — recipe-attached ("Swingarm", modeled in this document).
Construction recipe (the document's own serialized feature program — sketch geometry with constraints, then the solid features built on it; lengths are millimeters unless a unit is written):

FEATURE [Sketcher::SketchObject] Sketch032
  FullyConstrained = true
  MapMode = 5
  Placement = pos=(0,0,0) rot=(1,0,0;1.5708rad)
  Support = -> [XZ_Plane015]
  sketch-geometry (4):
    g0: ArcOfCircle CenterX=0 CenterY=0 CenterZ=0 NormalX=0 NormalY=0 NormalZ=1 AngleXU=0 Radius=6.35 StartAngle=0 EndAngle=3.14159
    g1: LineSegment StartX=-6.35 StartY=8e-16 StartZ=0 EndX=-6.35 EndY=-6.35 EndZ=0
    g2: LineSegment StartX=-6.35 StartY=-6.35 StartZ=0 EndX=6.35 EndY=-6.35 EndZ=0
    g3: LineSegment StartX=6.35 StartY=-6.35 StartZ=0 EndX=6.35 EndY=0 EndZ=0
  constraints (12):
    c: Coincident(g0,g-1)
    c: PointOnObject(g0,g-1)
    c: PointOnObject(g0,g-1)
    c: Coincident(g1,g0)
    c: Vertical(g1)
    c: Coincident(g2,g1)
    c: Horizontal(g2)
    c: Coincident(g3,g2)
    c: Coincident(g3,g0)
    c: Vertical(g3)
    c: Distance(g2) = 12.7
    c: Distance(g3) = 6.35
FEATURE [PartDesign::Pad] Pad015
  Direction = (0,-1,-2e-16)
  Length = 12.7
  Length2 = 10
  Placement = pos=(0,0,0) rot=(1,0,0;1.5708rad)
  Profile = -> Sketch032
  ReferenceAxis = -> Sketch032 [N_Axis]
  Type = 0
FEATURE [PartDesign::Plane] DatumPlane002
  AttachmentOffset = pos=(0,0,-6.35) rot=(0,0,1;0rad)
  Length = 60
  MapMode = 5
  Placement = pos=(0,0,0) rot=(1,0,0;3.14159rad)
  ResizeMode = 0
  Support = -> [Pad015]
  Width = 60
FEATURE [Sketcher::SketchObject] Sketch033
  ExternalGeometry = -> [Pad015]
  FullyConstrained = true
  MapMode = 5
  Placement = pos=(0,0,0) rot=(1,0,0;3.14159rad)
  Support = -> [DatumPlane002]
  sketch-geometry (2):
    g0: Circle CenterX=0 CenterY=6.35 CenterZ=0 NormalX=0 NormalY=0 NormalZ=1 AngleXU=0 Radius=3.8862
    g1: GeomPoint X=0 Y=12.7 Z=0
  constraints (4):
    c: PointOnObject(g1,g-3)
    c: PointOnObject(g1,g-2)
    c: Symmetric(g1,g-1,g0)
    c: Diameter(g0) = 7.7724
FEATURE [PartDesign::Pad] Pad016
  BaseFeature = -> Pad015
  Direction = (0,-2e-16,-1)
  Length = 25.4
  Length2 = 10
  Placement = pos=(0,0,0) rot=(1,0,0;1.5708rad)
  Profile = -> Sketch033
  ReferenceAxis = -> Sketch033 [N_Axis]
  Reversed = true
  Type = 0
FEATURE [Sketcher::SketchObject] Sketch034
  FullyConstrained = true
  MapMode = 5
  Placement = pos=(0,-12.7,1.4e-15) rot=(1,0,0;1.5708rad)
  Support = -> [Pad016]
  sketch-geometry (3):
    g0: ArcOfCircle CenterX=0 CenterY=0 CenterZ=0 NormalX=0 NormalY=0 NormalZ=1 AngleXU=0 Radius=3.0988 StartAngle=2.13269 EndAngle=7.29209
    g1: LineSegment StartX=-1.651 StartY=2.62236 StartZ=0 EndX=1.651 EndY=2.62236 EndZ=0
    g2: LineSegment StartX=0 StartY=2.62236 StartZ=0 EndX=0 EndY=-3.0988 EndZ=0
  constraints (10):
    c: Coincident(g0,g-1)
    c: Coincident(g1,g0)
    c: Coincident(g1,g0)
    c: Horizontal(g1)
    c: Radius(g0) = 3.0988
    c: PointOnObject(g2,g1)
    c: PointOnObject(g2,g0)
    c: Vertical(g2)
    c: PointOnObject(g0,g2)
    c: Distance(g1) = 3.302
FEATURE [PartDesign::Pocket] Pocket016
  BaseFeature = -> Pad016
  Direction = (0,1,-2e-16)
  Length = 5
  Length2 = 5
  Placement = pos=(0,0,0) rot=(1,0,0;1.5708rad)
  Profile = -> Sketch034
  ReferenceAxis = -> Sketch034 [N_Axis]
  Type = 1
FEATURE [PartDesign::Body] Body014  label="Swingarm"
  Group = -> [Sketch032,Pad015,DatumPlane002,Sketch033,Pad016,Sketch034,Pocket016]
  Origin = -> Origin015
  Tip = -> Pocket016
PROVENANCE & LICENSES
A FreeCAD (.FCStd) document from a public repository crawl; recipes are the document's own serialized feature recipes (and, for linked parts, companion documents' recipes).
License: as declared in the source repository (recorded in the dataset sidecar).
